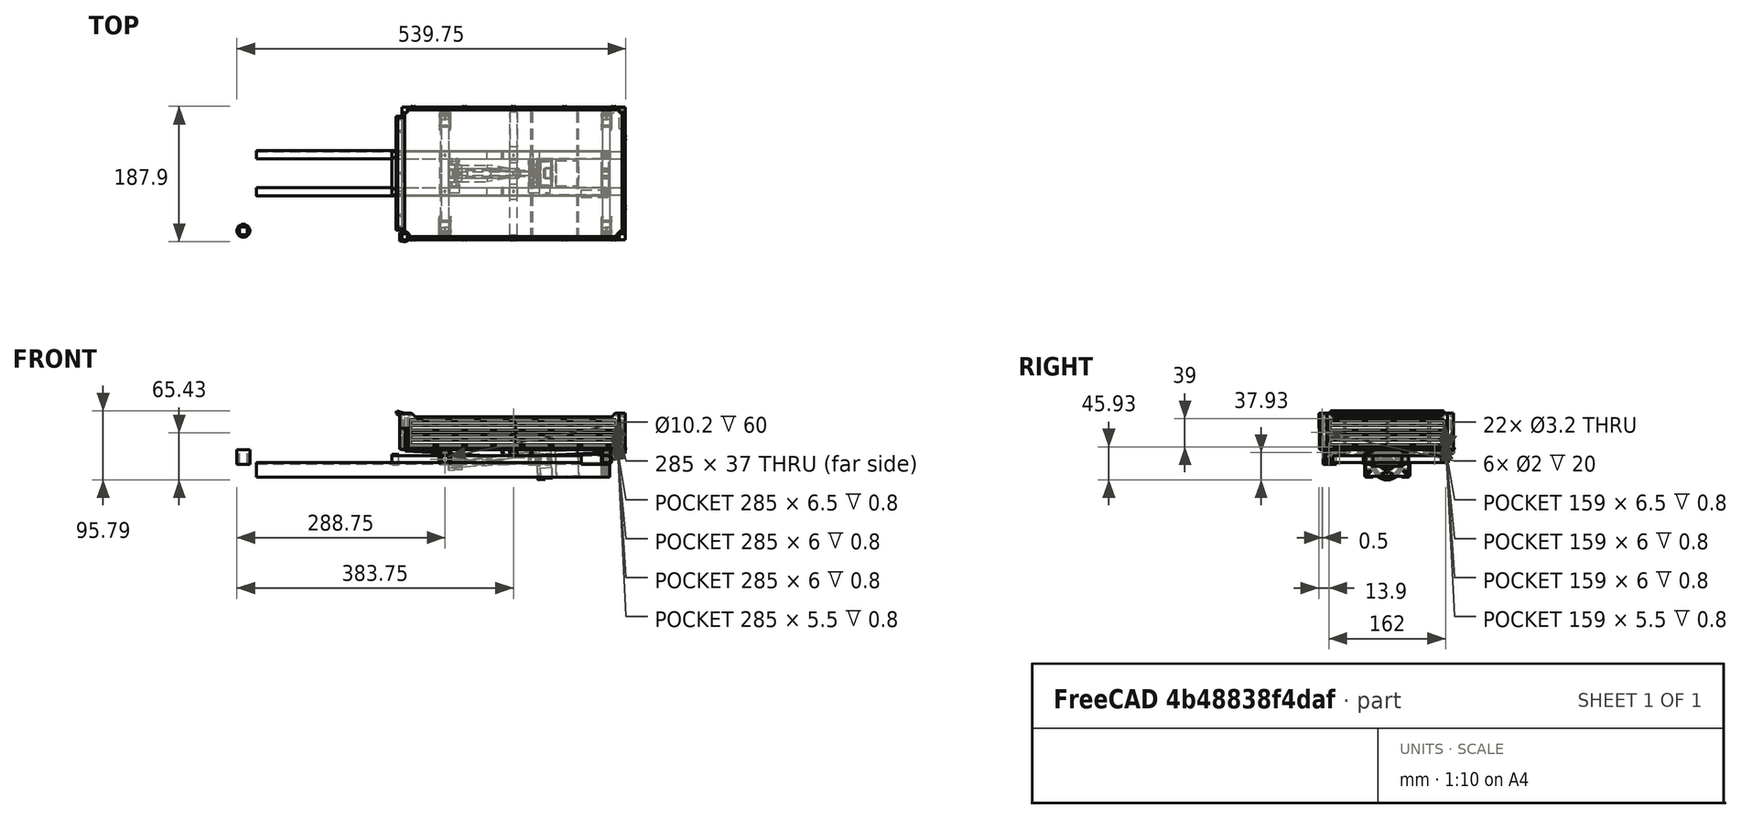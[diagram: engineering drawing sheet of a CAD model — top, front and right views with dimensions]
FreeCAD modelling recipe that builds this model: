
FCSTD DOCUMENT  (FreeCAD 0.16R6348 (Git))
Label: kipper-01
License: All rights reserved
LicenseURL: http://en.wikipedia.org/wiki/All_rights_reserved
objects: Part::Box×218, Part::Cylinder×187, Part::MultiFuse×136, Part::Cut×129, Part::Chamfer×84, Part::Fillet×63, Part::Mirroring×11, App::DocumentObjectGroup×1, Part::RegularPolygon×1, Part::Feature×1, Part::Extrusion×1
note: 831 computed .brp shape members not serialized (recipe doc carries the construction recipe); baked Part::Feature solids carry a one-line shape summary decoded from their .brp

FEATURE [Part::Box] Box416  label="Cube641"
  Height = 20
  Length = 490
  Placement = pos=(0,0,-92) rot=(0,0,1;0rad)
  Width = 11.5
FEATURE [Part::Box] Box417  label="Cube642"
  Height = 17
  Length = 490
  Placement = pos=(0,1.5,-90.5) rot=(0,0,1;0rad)
  Width = 10
FEATURE [Part::Cut] Cut429  label="Cut769"
  Base = -> Box416
  Tool = -> Box417
FEATURE [Part::Fillet] Fillet268
  Base = -> Cut429
  Edges = 2 edges r=3: [Edge11,Edge23]
  Placement = pos=(0,-1.5,0) rot=(0,0,1;0rad)
FEATURE [Part::Box] Box418  label="Cube643"
  Height = 20
  Length = 490
  Placement = pos=(0,0,-92) rot=(0,0,1;0rad)
  Width = 11.5
FEATURE [Part::Box] Box419  label="Cube644"
  Height = 17
  Length = 490
  Placement = pos=(0,1.5,-90.5) rot=(0,0,1;0rad)
  Width = 10
FEATURE [Part::Cut] Cut430  label="Cut770"
  Base = -> Box418
  Tool = -> Box419
FEATURE [Part::Fillet] Fillet269
  Base = -> Cut430
  Edges = 2 edges r=3: [Edge11,Edge23]
FEATURE [Part::Mirroring] Part__Mirroring036  label="Fillet269 (Mirror #29)"
  Base = (0,0,0)
  Normal = (0,1,0)
  Placement = pos=(0,61.5,0) rot=(0,0,1;0rad)
  Source = -> Fillet269
FEATURE [Part::MultiFuse] Fusion231  label="frame-00"
  Placement = pos=(23.5,55,74) rot=(0,0,1;0rad)
  Shapes = -> [Part__Mirroring036,Fillet268]
FEATURE [Part::Cylinder] Cylinder1019  label="Cylinder1221"
  Angle = 360
  Height = 170
  Placement = pos=(509,170,7) rot=(1,0,0;1.5708rad)
  Radius = 5
FEATURE [Part::Box] Box600  label="Cube789"
  Height = 8
  Length = 11
  Placement = pos=(279.5,0,12) rot=(0,0,1;0rad)
  Width = 170
FEATURE [Part::Box] Box601  label="Cube790"
  Height = 8
  Length = 10
  Placement = pos=(504,0,12) rot=(0,0,1;0rad)
  Width = 170
FEATURE [Part::Box] Box602  label="Cube791"
  Height = 10
  Length = 224
  Placement = pos=(290,55,2) rot=(0,0,1;0rad)
  Width = 10
FEATURE [Part::Box] Box603  label="Cube792"
  Height = 10
  Length = 224
  Placement = pos=(290,105,2) rot=(0,0,1;0rad)
  Width = 10
FEATURE [Part::Box] Box604  label="Cube793"
  Height = 8
  Length = 300
  Placement = pos=(230,55,12) rot=(0,0,1;0rad)
  Width = 10
FEATURE [Part::Box] Box605  label="Cube794"
  Height = 8
  Length = 300
  Placement = pos=(229,55,10) rot=(0,1,0;0.05236rad)
  Width = 10
FEATURE [Part::Box] Box606  label="Cube795"
  Height = 8
  Length = 300
  Placement = pos=(230,55,10) rot=(0,1,0;0.05236rad)
  Width = 10
FEATURE [Part::Mirroring] Part__Mirroring  label="Cube795 (Mirror #2)"
  Base = (0,0,0)
  Normal = (1,0,0)
  Placement = pos=(761,0,0) rot=(0,0,1;0rad)
  Source = -> Box606
FEATURE [Part::MultiFuse] Fusion
  Shapes = -> [Box605,Part__Mirroring]
FEATURE [Part::Cut] Cut
  Base = -> Box604
  Tool = -> Fusion
FEATURE [Part::Box] Box607  label="Cube796"
  Height = 8
  Length = 10
  Placement = pos=(375,0,12) rot=(0,0,1;0rad)
  Width = 170
FEATURE [Part::Box] Box608  label="Cube797"
  Height = 8
  Length = 10
  Placement = pos=(375,-1,10) rot=(-1,0,0;0.122173rad)
  Width = 170
FEATURE [Part::Box] Box609  label="Cube798"
  Height = 8
  Length = 10
  Placement = pos=(375,-1,10) rot=(-1,0,0;0.122173rad)
  Width = 170
FEATURE [Part::Mirroring] Part__Mirroring037  label="Cube798 (Mirror #3)"
  Base = (0,0,0)
  Normal = (0,1,0)
  Placement = pos=(0,170,0) rot=(0,0,1;0rad)
  Source = -> Box609
FEATURE [Part::MultiFuse] Fusion232
  Shapes = -> [Box608,Part__Mirroring037]
FEATURE [Part::Cut] Cut014188
  Base = -> Box607
  Tool = -> Fusion232
FEATURE [Part::Box] Box610  label="Cube799"
  Height = 8
  Length = 300
  Placement = pos=(230,55,12) rot=(0,0,1;0rad)
  Width = 10
FEATURE [Part::Box] Box611  label="Cube800"
  Height = 8
  Length = 300
  Placement = pos=(229,55,10) rot=(0,1,0;0.05236rad)
  Width = 10
FEATURE [Part::Box] Box612  label="Cube801"
  Height = 8
  Length = 300
  Placement = pos=(230,55,10) rot=(0,1,0;0.05236rad)
  Width = 10
FEATURE [Part::Mirroring] Part__Mirroring038  label="Cube795 (Mirror #2)001"
  Base = (0,0,0)
  Normal = (1,0,0)
  Placement = pos=(761,0,0) rot=(0,0,1;0rad)
  Source = -> Box612
FEATURE [Part::MultiFuse] Fusion233
  Shapes = -> [Box611,Part__Mirroring038]
FEATURE [Part::Cut] Cut014189
  Base = -> Box610
  Placement = pos=(0,50,0) rot=(0,0,1;0rad)
  Tool = -> Fusion233
FEATURE [Part::Box] Box112  label="Cube111"
  Height = 45
  Length = 4
  Placement = pos=(-4,-44,16) rot=(0,0,1;0rad)
  Width = 168
FEATURE [Part::Box] Box113  label="Cube112"
  Height = 33
  Length = 4
  Placement = pos=(-4,-40,22) rot=(0,0,1;0rad)
  Width = 160
FEATURE [Part::Cut] Cut166
  Base = -> Box112
  Tool = -> Box113
FEATURE [Part::Box] Box117  label="Cube116"
  Height = 7
  Length = 3
  Placement = pos=(-3,-40,35) rot=(0,0,1;0rad)
  Width = 160
FEATURE [Part::Chamfer] Chamfer048
  Base = -> Box117
  Edges = 2 edges r=1: [Edge2,Edge4]
  Placement = pos=(0,0,0.5) rot=(0,0,1;0rad)
FEATURE [Part::Cylinder] Cylinder283  label="Cylinder465"
  Angle = 360
  Height = 3.8
  Placement = pos=(-1.5,135,55) rot=(1,0,0;1.5708rad)
  Radius = 0.9
FEATURE [Part::Cylinder] Cylinder284  label="Cylinder466"
  Angle = 360
  Height = 3.8
  Placement = pos=(-1.5,135,25) rot=(1,0,0;1.5708rad)
  Radius = 0.9
FEATURE [Part::MultiFuse] Fusion161
  Placement = pos=(0,-11,0) rot=(0,0,1;0rad)
  Shapes = -> [Cylinder283,Cylinder284]
FEATURE [Part::Cylinder] Cylinder285  label="Cylinder467"
  Angle = 360
  Height = 3.8
  Placement = pos=(-1.5,135,25) rot=(1,0,0;1.5708rad)
  Radius = 0.9
FEATURE [Part::MultiFuse] Fusion162
  Placement = pos=(0,-175.2,0) rot=(0,0,1;0rad)
  Shapes = -> [Cylinder285]
FEATURE [Part::MultiFuse] Fusion163
  Placement = pos=(229,45,5) rot=(0,0,1;0rad)
  Shapes = -> [Fusion162,Fusion161]
FEATURE [Part::Box] Box121  label="kipper-front-wall-frame-ALU"
  Height = 45
  Length = 0.6
  Placement = pos=(228.4,1,21) rot=(0,0,1;0rad)
  Width = 168
FEATURE [Part::Cylinder] Cylinder290  label="Cylinder472"
  Angle = 360
  Height = 10
  Placement = pos=(227.5,111,16) rot=(0,0,1;0rad)
  Radius = 0.9
FEATURE [Part::Cylinder] Cylinder291  label="Cylinder473"
  Angle = 360
  Height = 10
  Placement = pos=(227.5,60,16) rot=(0,0,1;0rad)
  Radius = 0.9
FEATURE [Part::MultiFuse] Fusion170
  Shapes = -> [Cylinder291,Cylinder290]
FEATURE [Part::Box] Box613  label="kipper-plane002"
  Height = 1
  Length = 310
  Placement = pos=(225,-7,20) rot=(0,0,1;0rad)
  Width = 184
FEATURE [Part::Chamfer] Chamfer
  Base = -> Cut166
  Edges = 2 edges r=2: [Edge5,Edge7]
FEATURE [Part::Box] Box614  label="Cube802"
  Height = 1
  Length = 1
  Placement = pos=(-1,-40,28.5) rot=(0,0,1;0rad)
  Width = 160
FEATURE [Part::Chamfer] Chamfer064
  Base = -> Box614
  Edges = 2 edges r=0.2: [Edge2,Edge4]
  Placement = pos=(-0.6,0,0) rot=(0,0,1;0rad)
FEATURE [Part::Box] Box615  label="Cube803"
  Height = 1
  Length = 1
  Placement = pos=(-1,-40,28.5) rot=(0,0,1;0rad)
  Width = 160
FEATURE [Part::Chamfer] Chamfer065
  Base = -> Box615
  Edges = 2 edges r=0.2: [Edge2,Edge4]
  Placement = pos=(-0.6,0,20) rot=(0,0,1;0rad)
FEATURE [Part::MultiFuse] Fusion234
  Placement = pos=(229,45,5) rot=(0,0,1;0rad)
  Shapes = -> [Chamfer048,Chamfer064,Chamfer,Chamfer065]
FEATURE [Part::Box] Box111  label="Cube110"
  Height = 50
  Length = 8
  Placement = pos=(-2,124,15) rot=(0,0,1;0rad)
  Width = 8
FEATURE [Part::Box] Box122  label="Cube121"
  Height = 50
  Length = 8
  Placement = pos=(-2,-52,15) rot=(0,0,1;0rad)
  Width = 8
FEATURE [Part::MultiFuse] Fusion183
  Placement = pos=(227,45,6) rot=(0,0,1;0rad)
  Shapes = -> [Box111,Box122]
FEATURE [Part::Box] Box616  label="Cube804"
  Height = 50
  Length = 8
  Placement = pos=(-2,124,15) rot=(0,0,1;0rad)
  Width = 8
FEATURE [Part::Box] Box617  label="Cube805"
  Height = 50
  Length = 8
  Placement = pos=(-2,-52,15) rot=(0,0,1;0rad)
  Width = 8
FEATURE [Part::MultiFuse] Fusion235
  Placement = pos=(529,45,6) rot=(0,0,1;0rad)
  Shapes = -> [Box616,Box617]
FEATURE [Part::MultiFuse] Fusion236  label="kipper-walls-supports-ALU"
  Shapes = -> [Fusion235,Fusion183]
FEATURE [Part::Box] Box618  label="Cube806"
  Height = 45
  Length = 4
  Placement = pos=(-4,-44,16) rot=(0,0,1;0rad)
  Width = 293
FEATURE [Part::Box] Box619  label="Cube807"
  Height = 33
  Length = 4
  Placement = pos=(-4,-40,22) rot=(0,0,1;0rad)
  Width = 285
FEATURE [Part::Cut] Cut014193
  Base = -> Box618
  Tool = -> Box619
FEATURE [Part::Box] Box620  label="Cube808"
  Height = 7
  Length = 3
  Placement = pos=(-3,-40,35) rot=(0,0,1;0rad)
  Width = 286
FEATURE [Part::Chamfer] Chamfer066
  Base = -> Box620
  Edges = 2 edges r=1: [Edge2,Edge4]
  Placement = pos=(0,0,0.5) rot=(0,0,1;0rad)
FEATURE [Part::Chamfer] Chamfer067
  Base = -> Cut014193
  Edges = 2 edges r=2: [Edge5,Edge7]
FEATURE [Part::Box] Box621  label="Cube809"
  Height = 1
  Length = 1
  Placement = pos=(-1,-40,28.5) rot=(0,0,1;0rad)
  Width = 286
FEATURE [Part::Chamfer] Chamfer068
  Base = -> Box621
  Edges = 2 edges r=0.2: [Edge2,Edge4]
  Placement = pos=(-0.6,0,0) rot=(0,0,1;0rad)
FEATURE [Part::Box] Box622  label="Cube810"
  Height = 1
  Length = 1
  Placement = pos=(-1,-40,28.5) rot=(0,0,1;0rad)
  Width = 286
FEATURE [Part::Chamfer] Chamfer069
  Base = -> Box622
  Edges = 2 edges r=0.2: [Edge2,Edge4]
  Placement = pos=(-0.6,0,20) rot=(0,0,1;0rad)
FEATURE [Part::Box] Box623  label="kipper-side-left-wall-frame-ALU"
  Height = 42
  Length = 0.6
  Placement = pos=(526,-3.6,24) rot=(0,0,1;1.5708rad)
  Width = 292
FEATURE [Part::Box] Box158  label="Cube157"
  Height = 4
  Length = 4
  Placement = pos=(58,-53.5,14) rot=(0,0,1;0rad)
  Width = 1
FEATURE [Part::Box] Box159  label="Cube158"
  Height = 4
  Length = 6
  Placement = pos=(57,-53,14) rot=(0,0,1;0rad)
  Width = 1
FEATURE [Part::Chamfer] Chamfer059
  Base = -> Box159
  Edges = 1 edges r=0.99: [Edge10]
FEATURE [Part::Fillet] Fillet020
  Base = -> Chamfer059
  Edges = 1 edges r=0.99: [Edge8]
FEATURE [Part::Cut] Cut188
  Base = -> Fillet020
  Placement = pos=(181,45,6) rot=(0,0,1;0rad)
  Tool = -> Box158
FEATURE [Part::Box] Box160  label="Cube159"
  Height = 4
  Length = 6
  Placement = pos=(57,-53,14) rot=(0,0,1;0rad)
  Width = 1
FEATURE [Part::Chamfer] Chamfer060
  Base = -> Box160
  Edges = 1 edges r=0.99: [Edge10]
FEATURE [Part::Fillet] Fillet021
  Base = -> Chamfer060
  Edges = 1 edges r=0.99: [Edge8]
FEATURE [Part::Box] Box161  label="Cube160"
  Height = 4
  Length = 4
  Placement = pos=(58,-53.5,14) rot=(0,0,1;0rad)
  Width = 1
FEATURE [Part::Cut] Cut189
  Base = -> Fillet021
  Placement = pos=(320,45,6) rot=(0,0,1;0rad)
  Tool = -> Box161
FEATURE [Part::Box] Box162  label="Cube161"
  Height = 4
  Length = 6
  Placement = pos=(57,-53,14) rot=(0,0,1;0rad)
  Width = 1
FEATURE [Part::Chamfer] Chamfer061
  Base = -> Box162
  Edges = 1 edges r=0.99: [Edge10]
FEATURE [Part::Fillet] Fillet022
  Base = -> Chamfer061
  Edges = 1 edges r=0.99: [Edge8]
FEATURE [Part::Box] Box163  label="Cube162"
  Height = 4
  Length = 4
  Placement = pos=(58,-53.5,14) rot=(0,0,1;0rad)
  Width = 1
FEATURE [Part::Cut] Cut190
  Base = -> Fillet022
  Placement = pos=(252,45,6) rot=(0,0,1;0rad)
  Tool = -> Box163
FEATURE [Part::Box] Box164  label="Cube163"
  Height = 4
  Length = 6
  Placement = pos=(57,-53,14) rot=(0,0,1;0rad)
  Width = 1
FEATURE [Part::Chamfer] Chamfer062
  Base = -> Box164
  Edges = 1 edges r=0.99: [Edge10]
FEATURE [Part::Fillet] Fillet023
  Base = -> Chamfer062
  Edges = 1 edges r=0.99: [Edge8]
FEATURE [Part::Box] Box165  label="Cube164"
  Height = 4
  Length = 4
  Placement = pos=(58,-53.5,14) rot=(0,0,1;0rad)
  Width = 1
FEATURE [Part::Cut] Cut191
  Base = -> Fillet023
  Placement = pos=(391,45,6) rot=(0,0,1;0rad)
  Tool = -> Box165
FEATURE [Part::Box] Box166  label="Cube165"
  Height = 4
  Length = 6
  Placement = pos=(57,-53,14) rot=(0,0,1;0rad)
  Width = 1
FEATURE [Part::Chamfer] Chamfer063
  Base = -> Box166
  Edges = 1 edges r=0.99: [Edge10]
FEATURE [Part::Fillet] Fillet024
  Base = -> Chamfer063
  Edges = 1 edges r=0.99: [Edge8]
FEATURE [Part::Box] Box167  label="Cube166"
  Height = 4
  Length = 4
  Placement = pos=(58,-53.5,14) rot=(0,0,1;0rad)
  Width = 1
FEATURE [Part::Cut] Cut192
  Base = -> Fillet024
  Placement = pos=(459,45,6) rot=(0,0,1;0rad)
  Tool = -> Box167
FEATURE [Part::MultiFuse] Fusion245
  Shapes = -> [Cut188,Cut189,Cut191,Cut190,Cut192]
FEATURE [Part::Box] Box624  label="Cube811"
  Height = 45
  Length = 4
  Placement = pos=(-4,-44,16) rot=(0,0,1;0rad)
  Width = 167
FEATURE [Part::Box] Box625  label="Cube812"
  Height = 33
  Length = 4
  Placement = pos=(-4,-40,22) rot=(0,0,1;0rad)
  Width = 159
FEATURE [Part::Cut] Cut014194
  Base = -> Box624
  Tool = -> Box625
FEATURE [Part::Box] Box626  label="Cube813"
  Height = 7
  Length = 3
  Placement = pos=(-3,-40,35) rot=(0,0,1;0rad)
  Width = 160
FEATURE [Part::Chamfer] Chamfer070
  Base = -> Box626
  Edges = 2 edges r=1: [Edge2,Edge4]
  Placement = pos=(0,0,0.5) rot=(0,0,1;0rad)
FEATURE [Part::Cylinder] Cylinder1025  label="Cylinder1222"
  Angle = 360
  Height = 5
  Placement = pos=(533,6,69) rot=(1,0,0;1.5708rad)
  Radius = 0.9
FEATURE [Part::Cylinder] Cylinder1026  label="Cylinder1223"
  Angle = 360
  Height = 5
  Placement = pos=(533,168,69) rot=(1,0,0;1.5708rad)
  Radius = 0.9
FEATURE [Part::Chamfer] Chamfer071
  Base = -> Cut014194
  Edges = 2 edges r=2: [Edge5,Edge7]
FEATURE [Part::Box] Box627  label="Cube814"
  Height = 1
  Length = 1
  Placement = pos=(-1,-40,28.5) rot=(0,0,1;0rad)
  Width = 160
FEATURE [Part::Chamfer] Chamfer072
  Base = -> Box627
  Edges = 2 edges r=0.2: [Edge2,Edge4]
  Placement = pos=(-0.6,0,0) rot=(0,0,1;0rad)
FEATURE [Part::Box] Box628  label="Cube815"
  Height = 1
  Length = 1
  Placement = pos=(-1,-40,28.5) rot=(0,0,1;0rad)
  Width = 160
FEATURE [Part::Chamfer] Chamfer073
  Base = -> Box628
  Edges = 2 edges r=0.2: [Edge2,Edge4]
  Placement = pos=(-0.6,0,20) rot=(0,0,1;0rad)
FEATURE [Part::MultiFuse] Fusion251
  Placement = pos=(229,45,5) rot=(0,0,1;0rad)
  Shapes = -> [Chamfer070,Chamfer072,Chamfer071,Chamfer073]
FEATURE [Part::MultiFuse] Fusion256
  Placement = pos=(0,0,-0.5) rot=(0,0,1;0rad)
  Shapes = -> [Cylinder1025,Cylinder1026]
FEATURE [Part::Mirroring] Part__Mirroring039  label="Fusion251 (Mirror #5)"
  Base = (0,0,0)
  Normal = (1,0,0)
  Placement = pos=(760,0,0) rot=(0,0,1;0rad)
  Source = -> Fusion251
FEATURE [Part::Box] Box114  label="Cube113"
  Height = 41
  Length = 6
  Placement = pos=(223,25,21) rot=(0,0,1;0rad)
  Width = 3
FEATURE [Part::Chamfer] Chamfer076
  Base = -> Box114
  Edges = 1 edges: [Edge2 r1=8 r2=3]
FEATURE [Part::Box] Box629  label="Cube816"
  Height = 41
  Length = 6
  Placement = pos=(223,25,21) rot=(0,0,1;0rad)
  Width = 3
FEATURE [Part::Chamfer] Chamfer077
  Base = -> Box629
  Edges = 1 edges: [Edge2 r1=8 r2=3]
  Placement = pos=(0,117,0) rot=(0,0,1;0rad)
FEATURE [Part::Box] Box630  label="Cube817"
  Height = 41
  Length = 6
  Placement = pos=(223,25,21) rot=(0,0,1;0rad)
  Width = 3
FEATURE [Part::Chamfer] Chamfer078
  Base = -> Box630
  Edges = 1 edges: [Edge2 r1=8 r2=3]
  Placement = pos=(0,59,0) rot=(0,0,1;0rad)
FEATURE [Part::Cylinder] Cylinder1036  label="Cylinder1224"
  Angle = 360
  Height = 20
  Placement = pos=(10.5,10.5,0) rot=(0,0,1;0rad)
  Radius = 0.55
FEATURE [Part::Box] Box631  label="Cube818"
  Height = 20
  Length = 10.5
  Width = 10.5
FEATURE [Part::Cylinder] Cylinder1037  label="Cylinder1225"
  Angle = 360
  Height = 20
  Placement = pos=(4.1,4.1,0) rot=(0,0,1;0rad)
  Radius = 7
FEATURE [Part::Box] Box632  label="Cube819"
  Height = 20
  Length = 8.2
  Width = 8.2
FEATURE [Part::Cut] Cut014197  label="square-lathe-8mm-ADAPT"
  Base = -> Cylinder1037
  Placement = pos=(225,-7,50) rot=(0,0,1;0rad)
  Tool = -> Box632
FEATURE [Part::Box] Box633  label="Cube820"
  Height = 5
  Length = 4
  Placement = pos=(531,1,66) rot=(0,0,1;0rad)
  Width = 10
FEATURE [Part::Chamfer] Chamfer079
  Base = -> Box633
  Edges = 1 edges r=4.999: [Edge12]
FEATURE [Part::Box] Box634  label="Cube821"
  Height = 5
  Length = 4
  Placement = pos=(531,159,66) rot=(0,0,1;0rad)
  Width = 10
FEATURE [Part::Chamfer] Chamfer080
  Base = -> Box634
  Edges = 1 edges r=4.999: [Edge10]
  Placement = pos=(0,-1,0) rot=(0,0,1;0rad)
FEATURE [Part::Box] Box635  label="kipper-rear-wall-frame-ALU"
  Height = 45
  Length = 0.6
  Placement = pos=(531,1,21) rot=(0,0,1;0rad)
  Width = 167
FEATURE [Part::Box] Box636  label="Cube822"
  Height = 4
  Length = 4
  Placement = pos=(58,-53.5,14) rot=(0,0,1;0rad)
  Width = 1
FEATURE [Part::Box] Box637  label="Cube823"
  Height = 4
  Length = 6
  Placement = pos=(57,-53,14) rot=(0,0,1;0rad)
  Width = 1
FEATURE [Part::Chamfer] Chamfer081
  Base = -> Box637
  Edges = 1 edges r=0.99: [Edge10]
FEATURE [Part::Fillet] Fillet270
  Base = -> Chamfer081
  Edges = 1 edges r=0.99: [Edge8]
FEATURE [Part::Cut] Cut014199
  Base = -> Fillet270
  Placement = pos=(483,74,6) rot=(0,0,1;1.5708rad)
  Tool = -> Box636
FEATURE [Part::Box] Box638  label="Cube824"
  Height = 4
  Length = 4
  Placement = pos=(58,-53.5,14) rot=(0,0,1;0rad)
  Width = 1
FEATURE [Part::Box] Box639  label="Cube825"
  Height = 4
  Length = 6
  Placement = pos=(57,-53,14) rot=(0,0,1;0rad)
  Width = 1
FEATURE [Part::Chamfer] Chamfer082
  Base = -> Box639
  Edges = 1 edges r=0.99: [Edge10]
FEATURE [Part::Fillet] Fillet271
  Base = -> Chamfer082
  Edges = 1 edges r=0.99: [Edge8]
FEATURE [Part::Cut] Cut014200
  Base = -> Fillet271
  Placement = pos=(483,-23,6) rot=(0,0,1;1.5708rad)
  Tool = -> Box638
FEATURE [Part::Box] Box640  label="Cube826"
  Height = 5
  Length = 4
  Placement = pos=(531,1,66) rot=(0,0,1;0rad)
  Width = 10
FEATURE [Part::Chamfer] Chamfer083
  Base = -> Box640
  Edges = 1 edges r=4.999: [Edge12]
  Placement = pos=(232.5,528,0) rot=(0,0,-1;1.5708rad)
FEATURE [Part::Box] Box641  label="Cube827"
  Height = 5
  Length = 4
  Placement = pos=(531,159,66) rot=(0,0,1;0rad)
  Width = 10
FEATURE [Part::Chamfer] Chamfer084
  Base = -> Box641
  Edges = 1 edges r=4.999: [Edge10]
  Placement = pos=(357.5,528,0) rot=(0,0,-1;1.5708rad)
FEATURE [Part::Cylinder] Cylinder1048  label="Cylinder1226"
  Angle = 360
  Height = 5
  Placement = pos=(233.5,-5,68.5) rot=(0,1,0;1.5708rad)
  Radius = 0.9
FEATURE [Part::Cylinder] Cylinder1049  label="Cylinder1227"
  Angle = 360
  Height = 5
  Placement = pos=(521.5,-5,68.5) rot=(0,1,0;1.5708rad)
  Radius = 0.9
FEATURE [Part::MultiFuse] Fusion266
  Shapes = -> [Cylinder1048,Cylinder1049]
FEATURE [Part::MultiFuse] Fusion279  label="kipper-frame_"
  Shapes = -> [Cut014189,Cut014188,Cut,Box601,Box600]
FEATURE [Part::Cylinder] Cylinder1062  label="Cylinder1228"
  Angle = 360
  Height = 10
  Placement = pos=(285,8,10) rot=(0,0,1;0rad)
  Radius = 1.25
FEATURE [Part::Cylinder] Cylinder1063  label="Cylinder1229"
  Angle = 360
  Height = 10
  Placement = pos=(285,60,10) rot=(0,0,1;0rad)
  Radius = 1.25
FEATURE [Part::Cylinder] Cylinder1064  label="Cylinder1230"
  Angle = 360
  Height = 10
  Placement = pos=(285,162,10) rot=(0,0,1;0rad)
  Radius = 1.25
FEATURE [Part::Cylinder] Cylinder1065  label="Cylinder1231"
  Angle = 360
  Height = 10
  Placement = pos=(285,110,10) rot=(0,0,1;0rad)
  Radius = 1.25
FEATURE [Part::Cylinder] Cylinder1067  label="Cylinder1232"
  Angle = 360
  Height = 10
  Placement = pos=(380,60,10) rot=(0,0,1;0rad)
  Radius = 1.25
FEATURE [Part::Cylinder] Cylinder1069  label="Cylinder1233"
  Angle = 360
  Height = 10
  Placement = pos=(380,110,10) rot=(0,0,1;0rad)
  Radius = 1.25
FEATURE [Part::Cylinder] Cylinder1070  label="Cylinder1234"
  Angle = 360
  Height = 10
  Placement = pos=(509,8,10) rot=(0,0,1;0rad)
  Radius = 1.25
FEATURE [Part::Cylinder] Cylinder1071  label="Cylinder1235"
  Angle = 360
  Height = 10
  Placement = pos=(509,60,10) rot=(0,0,1;0rad)
  Radius = 1.25
FEATURE [Part::Cylinder] Cylinder1072  label="Cylinder1297"
  Angle = 360
  Height = 10
  Placement = pos=(509,162,10) rot=(0,0,1;0rad)
  Radius = 1.25
FEATURE [Part::Cylinder] Cylinder1073  label="Cylinder1298"
  Angle = 360
  Height = 10
  Placement = pos=(509,110,10) rot=(0,0,1;0rad)
  Radius = 1.25
FEATURE [Part::Cylinder] Cylinder1074  label="Cylinder1299"
  Angle = 360
  Height = 11
  Placement = pos=(279.5,4,16) rot=(0,1,0;1.5708rad)
  Radius = 1.25
FEATURE [Part::Cylinder] Cylinder1076  label="Cylinder1300"
  Angle = 360
  Height = 11
  Placement = pos=(279.5,19,16) rot=(0,1,0;1.5708rad)
  Radius = 1.25
FEATURE [Part::Cylinder] Cylinder1077  label="Cylinder1301"
  Angle = 360
  Height = 11
  Placement = pos=(503.5,19,16) rot=(0,1,0;1.5708rad)
  Radius = 1.25
FEATURE [Part::Cylinder] Cylinder1078  label="Cylinder1277"
  Angle = 360
  Height = 11
  Placement = pos=(503.5,4,16) rot=(0,1,0;1.5708rad)
  Radius = 1.25
FEATURE [Part::MultiFuse] Fusion282
  Shapes = -> [Cylinder1074,Cylinder1076,Cylinder1077,Cylinder1078]
FEATURE [Part::Cylinder] Cylinder1079  label="Cylinder1302"
  Angle = 360
  Height = 11
  Placement = pos=(279.5,4,16) rot=(0,1,0;1.5708rad)
  Radius = 1.25
FEATURE [Part::Cylinder] Cylinder1080  label="Cylinder1243"
  Angle = 360
  Height = 11
  Placement = pos=(279.5,19,16) rot=(0,1,0;1.5708rad)
  Radius = 1.25
FEATURE [Part::Cylinder] Cylinder1081  label="Cylinder1244"
  Angle = 360
  Height = 11
  Placement = pos=(503.5,19,16) rot=(0,1,0;1.5708rad)
  Radius = 1.25
FEATURE [Part::Cylinder] Cylinder1082  label="Cylinder1245"
  Angle = 360
  Height = 11
  Placement = pos=(503.5,4,16) rot=(0,1,0;1.5708rad)
  Radius = 1.25
FEATURE [Part::MultiFuse] Fusion283
  Placement = pos=(0,147,0) rot=(0,0,1;0rad)
  Shapes = -> [Cylinder1079,Cylinder1080,Cylinder1081,Cylinder1082]
FEATURE [Part::Cylinder] Cylinder1088  label="Cylinder1251"
  Angle = 360
  Height = 10
  Placement = pos=(405,105,15) rot=(-1,0,0;1.5708rad)
  Radius = 1.25
FEATURE [Part::Cylinder] Cylinder1089  label="Cylinder1252"
  Angle = 360
  Height = 10
  Placement = pos=(405,55,15) rot=(-1,0,0;1.5708rad)
  Radius = 1.25
FEATURE [Part::MultiFuse] Fusion285
  Shapes = -> [Cylinder1073,Cylinder1062,Cylinder1063,Cylinder1064,Cylinder1065,Cylinder1071,Cylinder1067,Cylinder1069,Cylinder1070,Cylinder1072]
FEATURE [Part::Box] Box  label="Cube"
  Height = 10
  Length = 145
  Placement = pos=(230,0,12) rot=(0,0,1;0rad)
  Width = 170
FEATURE [Part::Box] Box660  label="Cube845"
  Height = 10
  Length = 145
  Placement = pos=(385,0,12) rot=(0,0,1;0rad)
  Width = 170
FEATURE [Part::Box] Box661  label="Cube846"
  Height = 8
  Length = 11
  Placement = pos=(279.5,0,12) rot=(0,0,1;0rad)
  Width = 170
FEATURE [Part::Box] Box662  label="Cube847"
  Height = 8
  Length = 10
  Placement = pos=(504,0,12) rot=(0,0,1;0rad)
  Width = 170
FEATURE [Part::Box] Box663  label="Cube848"
  Height = 8
  Length = 300
  Placement = pos=(230,55,12) rot=(0,0,1;0rad)
  Width = 10
FEATURE [Part::Box] Box664  label="Cube849"
  Height = 8
  Length = 300
  Placement = pos=(229,55,10) rot=(0,1,0;0.05236rad)
  Width = 10
FEATURE [Part::Box] Box665  label="Cube850"
  Height = 8
  Length = 300
  Placement = pos=(230,55,10) rot=(0,1,0;0.05236rad)
  Width = 10
FEATURE [Part::Mirroring] Part__Mirroring041  label="Cube795 (Mirror #2)002"
  Base = (0,0,0)
  Normal = (1,0,0)
  Placement = pos=(761,0,0) rot=(0,0,1;0rad)
  Source = -> Box665
FEATURE [Part::MultiFuse] Fusion287
  Shapes = -> [Box664,Part__Mirroring041]
FEATURE [Part::Cut] Cut014212
  Base = -> Box663
  Tool = -> Fusion287
FEATURE [Part::Box] Box666  label="Cube851"
  Height = 8
  Length = 10
  Placement = pos=(375,0,12) rot=(0,0,1;0rad)
  Width = 170
FEATURE [Part::Box] Box667  label="Cube852"
  Height = 8
  Length = 10
  Placement = pos=(375,-1,10) rot=(-1,0,0;0.122173rad)
  Width = 170
FEATURE [Part::Box] Box668  label="Cube853"
  Height = 8
  Length = 10
  Placement = pos=(375,-1,10) rot=(-1,0,0;0.122173rad)
  Width = 170
FEATURE [Part::Mirroring] Part__Mirroring042  label="Cube798 (Mirror #3)001"
  Base = (0,0,0)
  Normal = (0,1,0)
  Placement = pos=(0,170,0) rot=(0,0,1;0rad)
  Source = -> Box668
FEATURE [Part::MultiFuse] Fusion288
  Shapes = -> [Box667,Part__Mirroring042]
FEATURE [Part::Cut] Cut014213
  Base = -> Box666
  Tool = -> Fusion288
FEATURE [Part::Box] Box669  label="Cube854"
  Height = 8
  Length = 300
  Placement = pos=(230,55,12) rot=(0,0,1;0rad)
  Width = 10
FEATURE [Part::Box] Box670  label="Cube855"
  Height = 8
  Length = 300
  Placement = pos=(229,55,10) rot=(0,1,0;0.05236rad)
  Width = 10
FEATURE [Part::Box] Box671  label="Cube856"
  Height = 8
  Length = 300
  Placement = pos=(230,55,10) rot=(0,1,0;0.05236rad)
  Width = 10
FEATURE [Part::Mirroring] Part__Mirroring043  label="Cube795 (Mirror #2)003"
  Base = (0,0,0)
  Normal = (1,0,0)
  Placement = pos=(761,0,0) rot=(0,0,1;0rad)
  Source = -> Box671
FEATURE [Part::MultiFuse] Fusion289
  Shapes = -> [Box670,Part__Mirroring043]
FEATURE [Part::Cut] Cut014214
  Base = -> Box669
  Placement = pos=(0,50,0) rot=(0,0,1;0rad)
  Tool = -> Fusion289
FEATURE [Part::MultiFuse] Fusion290  label="kipper-frame_001"
  Shapes = -> [Cut014214,Cut014213,Cut014212,Box662,Box661]
FEATURE [Part::Cylinder] Cylinder1090  label="Cylinder1253"
  Angle = 360
  Height = 10
  Placement = pos=(285,8,10) rot=(0,0,1;0rad)
  Radius = 1.25
FEATURE [Part::Cylinder] Cylinder1091  label="Cylinder1254"
  Angle = 360
  Height = 10
  Placement = pos=(285,60,10) rot=(0,0,1;0rad)
  Radius = 1.25
FEATURE [Part::Cylinder] Cylinder1092  label="Cylinder1255"
  Angle = 360
  Height = 10
  Placement = pos=(285,162,10) rot=(0,0,1;0rad)
  Radius = 1.25
FEATURE [Part::Cylinder] Cylinder1093  label="Cylinder1256"
  Angle = 360
  Height = 10
  Placement = pos=(285,110,10) rot=(0,0,1;0rad)
  Radius = 1.25
FEATURE [Part::Cylinder] Cylinder1094  label="Cylinder1257"
  Angle = 360
  Height = 10
  Placement = pos=(380,60,10) rot=(0,0,1;0rad)
  Radius = 1.25
FEATURE [Part::Cylinder] Cylinder1095  label="Cylinder1258"
  Angle = 360
  Height = 10
  Placement = pos=(380,110,10) rot=(0,0,1;0rad)
  Radius = 1.25
FEATURE [Part::Cylinder] Cylinder1096  label="Cylinder1259"
  Angle = 360
  Height = 10
  Placement = pos=(509,8,10) rot=(0,0,1;0rad)
  Radius = 1.25
FEATURE [Part::Cylinder] Cylinder1097  label="Cylinder1260"
  Angle = 360
  Height = 10
  Placement = pos=(509,60,10) rot=(0,0,1;0rad)
  Radius = 1.25
FEATURE [Part::Cylinder] Cylinder1098  label="Cylinder1261"
  Angle = 360
  Height = 10
  Placement = pos=(509,162,10) rot=(0,0,1;0rad)
  Radius = 1.25
FEATURE [Part::Cylinder] Cylinder1099  label="Cylinder1303"
  Angle = 360
  Height = 10
  Placement = pos=(509,110,10) rot=(0,0,1;0rad)
  Radius = 1.25
FEATURE [Part::Cylinder] Cylinder1100  label="Cylinder1304"
  Angle = 360
  Height = 11
  Placement = pos=(279.5,4,16) rot=(0,1,0;1.5708rad)
  Radius = 1.25
FEATURE [Part::Cylinder] Cylinder1101  label="Cylinder1305"
  Angle = 360
  Height = 11
  Placement = pos=(279.5,19,16) rot=(0,1,0;1.5708rad)
  Radius = 1.25
FEATURE [Part::Cylinder] Cylinder1102  label="Cylinder1306"
  Angle = 360
  Height = 11
  Placement = pos=(503.5,19,16) rot=(0,1,0;1.5708rad)
  Radius = 1.25
FEATURE [Part::Cylinder] Cylinder1103  label="Cylinder1307"
  Angle = 360
  Height = 11
  Placement = pos=(503.5,4,16) rot=(0,1,0;1.5708rad)
  Radius = 1.25
FEATURE [Part::MultiFuse] Fusion291
  Shapes = -> [Cylinder1100,Cylinder1101,Cylinder1102,Cylinder1103]
FEATURE [Part::Cylinder] Cylinder1104  label="Cylinder1308"
  Angle = 360
  Height = 11
  Placement = pos=(279.5,4,16) rot=(0,1,0;1.5708rad)
  Radius = 1.25
FEATURE [Part::Cylinder] Cylinder1105  label="Cylinder1309"
  Angle = 360
  Height = 11
  Placement = pos=(279.5,19,16) rot=(0,1,0;1.5708rad)
  Radius = 1.25
FEATURE [Part::Cylinder] Cylinder1106  label="Cylinder1310"
  Angle = 360
  Height = 11
  Placement = pos=(503.5,19,16) rot=(0,1,0;1.5708rad)
  Radius = 1.25
FEATURE [Part::Cylinder] Cylinder1107  label="Cylinder1311"
  Angle = 360
  Height = 11
  Placement = pos=(503.5,4,16) rot=(0,1,0;1.5708rad)
  Radius = 1.25
FEATURE [Part::MultiFuse] Fusion292
  Placement = pos=(0,147,0) rot=(0,0,1;0rad)
  Shapes = -> [Cylinder1104,Cylinder1105,Cylinder1106,Cylinder1107]
FEATURE [Part::Cylinder] Cylinder1111  label="Cylinder1312"
  Angle = 360
  Height = 10
  Placement = pos=(365,55,16) rot=(-1,0,0;1.5708rad)
  Radius = 1.25
FEATURE [Part::Cylinder] Cylinder1112  label="Cylinder1313"
  Angle = 360
  Height = 10
  Placement = pos=(365,105,16) rot=(-1,0,0;1.5708rad)
  Radius = 1.25
FEATURE [Part::MultiFuse] Fusion294
  Shapes = -> [Cylinder1099,Cylinder1090,Cylinder1091,Cylinder1092,Cylinder1093,Cylinder1097,Cylinder1094,Cylinder1095,Cylinder1096,Cylinder1098]
FEATURE [Part::Box] Box672  label="Cube857"
  Height = 10
  Length = 10
  Placement = pos=(375,0,12) rot=(0,0,1;0rad)
  Width = 55
FEATURE [Part::Box] Box673  label="Cube858"
  Height = 10
  Length = 10
  Placement = pos=(375,65,12) rot=(0,0,1;0rad)
  Width = 40
FEATURE [Part::Box] Box674  label="Cube859"
  Height = 10
  Length = 10
  Placement = pos=(375,115,12) rot=(0,0,1;0rad)
  Width = 55
FEATURE [Part::Box] Box675  label="Cube860"
  Height = 4.5
  Length = 10
  Placement = pos=(375,55,12) rot=(0,0,1;0rad)
  Width = 60
FEATURE [Part::MultiFuse] Fusion296
  Shapes = -> [Box672,Box674,Box675,Box673]
FEATURE [Part::Box] Box676  label="Cube861"
  Height = 4
  Length = 11
  Placement = pos=(374.5,54.5,16) rot=(0,0,1;0rad)
  Width = 11
FEATURE [Part::Box] Box677  label="Cube862"
  Height = 4
  Length = 11
  Placement = pos=(374.5,104.5,16) rot=(0,0,1;0rad)
  Width = 11
FEATURE [Part::MultiFuse] Fusion297
  Shapes = -> [Box677,Box676]
FEATURE [Part::Box] Box678  label="Cube863"
  Height = 4
  Length = 12
  Placement = pos=(217,6,70) rot=(0,1,0;0.261799rad)
  Width = 158
FEATURE [Part::Box] Box679  label="Cube864"
  Height = 4
  Length = 13
  Placement = pos=(218.588,8,70.6593) rot=(0,1,0;0.261799rad)
  Width = 154
FEATURE [Part::Box] Box680  label="Cube865"
  Height = 4
  Length = 4
  Placement = pos=(225,1,66) rot=(0,0,1;0rad)
  Width = 168
FEATURE [Part::Box] Box681  label="Cube866"
  Height = 4
  Length = 11
  Placement = pos=(218,6,66) rot=(0,0,1;0rad)
  Width = 4
FEATURE [Part::Chamfer] Chamfer097
  Base = -> Box681
  Edges = 1 edges: [Edge4 r1=3.99 r2=7]
  Placement = pos=(0,1,0) rot=(0,0,1;0rad)
FEATURE [Part::Box] Box682  label="Cube867"
  Height = 4
  Length = 11
  Placement = pos=(218,6,66) rot=(0,0,1;0rad)
  Width = 4
FEATURE [Part::Chamfer] Chamfer098
  Base = -> Box682
  Edges = 1 edges: [Edge4 r1=3.99 r2=7]
  Placement = pos=(0,153,0) rot=(0,0,1;0rad)
FEATURE [Part::Box] Box683  label="Cube868"
  Height = 4
  Length = 11
  Placement = pos=(218,6,66) rot=(0,0,1;0rad)
  Width = 4
FEATURE [Part::Chamfer] Chamfer099
  Base = -> Box683
  Edges = 1 edges: [Edge4 r1=3.99 r2=7]
  Placement = pos=(0,50,0) rot=(0,0,1;0rad)
FEATURE [Part::Box] Box684  label="Cube869"
  Height = 4
  Length = 11
  Placement = pos=(218,6,66) rot=(0,0,1;0rad)
  Width = 4
FEATURE [Part::Chamfer] Chamfer100
  Base = -> Box684
  Edges = 1 edges: [Edge4 r1=3.99 r2=7]
  Placement = pos=(0,104,0) rot=(0,0,1;0rad)
FEATURE [Part::Box] Box685  label="Cube870"
  Height = 10
  Length = 2
  Placement = pos=(229,6,63) rot=(0,0,1;0rad)
  Width = 158
FEATURE [Part::Box] Box703  label="Cube888"
  Height = 14
  Length = 40
  Placement = pos=(474,52,0) rot=(0,0,1;0rad)
  Width = 10
FEATURE [Part::Box] Box704  label="Cube889"
  Height = 10.2
  Length = 40
  Placement = pos=(474,55,1.9) rot=(0,0,1;0rad)
  Width = 10
FEATURE [Part::Cut] Cut014230
  Base = -> Box703
  Tool = -> Box704
FEATURE [Part::Cylinder] Cylinder1127  label="Cylinder1314"
  Angle = 360
  Height = 10
  Placement = pos=(509,58,7) rot=(1,0,0;1.5708rad)
  Radius = 1.5
FEATURE [Part::Cut] Cut014231  label="square-10mm-ending-HOLES"
  Base = -> Cut014230
  Tool = -> Cylinder1127
FEATURE [Part::Box] Box705  label="Cube890"
  Height = 50
  Length = 8.2
  Placement = pos=(224.9,-7,21) rot=(0,0,1;0rad)
  Width = 8
FEATURE [Part::Cylinder] Cylinder1128  label="Cylinder1315"
  Angle = 360
  Height = 10
  Placement = pos=(-1.5,135,25) rot=(1,0,0;1.5708rad)
  Radius = 1
FEATURE [Part::Cylinder] Cylinder1129  label="Cylinder1316"
  Angle = 360
  Height = 10
  Placement = pos=(-1.5,135,55) rot=(1,0,0;1.5708rad)
  Radius = 1
FEATURE [Part::MultiFuse] Fusion311
  Placement = pos=(229,-137,5) rot=(0,0,1;0rad)
  Shapes = -> [Cylinder1128,Cylinder1129]
FEATURE [Part::Cylinder] Cylinder1130  label="Cylinder1317"
  Angle = 360
  Height = 10
  Placement = pos=(220.5,-5,68.5) rot=(0,1,0;1.5708rad)
  Radius = 1
FEATURE [Part::Box] Box706  label="Cube891"
  Height = 50
  Length = 12
  Placement = pos=(223,-10,21) rot=(0,0,1;0rad)
  Width = 8
FEATURE [Part::Cut] Cut014232
  Base = -> Box706
  Tool = -> Box705
FEATURE [Part::Cylinder] Cylinder1131  label="Cylinder1318"
  Angle = 360
  Height = 10
  Placement = pos=(220.5,-1,68.5) rot=(0,1,0;1.5708rad)
  Radius = 1
FEATURE [Part::MultiFuse] Fusion312
  Shapes = -> [Cylinder1131,Cylinder1130]
FEATURE [Part::Cylinder] Cylinder1132  label="Cylinder1319"
  Angle = 360
  Height = 10
  Placement = pos=(-1.5,135,25) rot=(1,0,0;1.5708rad)
  Radius = 1
FEATURE [Part::Cylinder] Cylinder1133  label="Cylinder1320"
  Angle = 360
  Height = 10
  Placement = pos=(-1.5,135,55) rot=(1,0,0;1.5708rad)
  Radius = 1
FEATURE [Part::MultiFuse] Fusion313
  Placement = pos=(232,-137,5) rot=(0,0,1;0rad)
  Shapes = -> [Cylinder1132,Cylinder1133]
FEATURE [Part::MultiFuse] Fusion314
  Shapes = -> [Fusion311,Fusion313]
FEATURE [Part::Cut] Cut014233
  Base = -> Cut014232
  Placement = pos=(232,226,0) rot=(0,0,-1;1.5708rad)
  Tool = -> Fusion314
FEATURE [Part::Cut] Cut014234  label="square-8mm-supports-HOLES"
  Base = -> Cut014233
  Tool = -> Fusion312
FEATURE [Part::Box] Box707  label="Cube892"
  Height = 51
  Length = 149.5
  Placement = pos=(233.5,-8,20) rot=(0,0,1;0rad)
  Width = 5
FEATURE [Part::Box] Box708  label="Cube893"
  Height = 51
  Length = 143.5
  Placement = pos=(383,-8,20) rot=(0,0,1;0rad)
  Width = 5
FEATURE [Part::Box] Box728  label="Cube913"
  Height = 2
  Length = 30
  Placement = pos=(505,169,18) rot=(0,0,1;0rad)
  Width = 8
FEATURE [Part::Box] Box729  label="Cube914"
  Height = 2
  Length = 8
  Placement = pos=(527,147,18) rot=(0,0,1;0rad)
  Width = 30
FEATURE [Part::Cylinder] Cylinder1146  label="Cylinder1321"
  Angle = 360
  Height = 5
  Placement = pos=(531,173,15) rot=(0,0,1;0rad)
  Radius = 4
FEATURE [Part::Cylinder] Cylinder1147  label="Cylinder1322"
  Angle = 360
  Height = 10
  Placement = pos=(531,173,15) rot=(0,0,1;0rad)
  Radius = 1.5
FEATURE [Part::MultiFuse] Fusion330
  Shapes = -> [Box728,Cylinder1146,Box729]
FEATURE [Part::Cut] Cut014247  label="kipper-corners-HOLES"
  Base = -> Fusion330
  Tool = -> Cylinder1147
FEATURE [Part::Cylinder] Cylinder1148  label="Cylinder1323"
  Angle = 360
  Height = 20
  Placement = pos=(5.25,5.25,0) rot=(0,0,1;0rad)
  Radius = 9
FEATURE [Part::Cylinder] Cylinder1149  label="Cylinder1324"
  Angle = 360
  Height = 20
  Placement = pos=(0,10.5,0) rot=(0,0,1;0rad)
  Radius = 0.55
FEATURE [Part::Cylinder] Cylinder1150  label="Cylinder1325"
  Angle = 360
  Height = 20
  Radius = 0.55
FEATURE [Part::Cylinder] Cylinder1151  label="Cylinder1326"
  Angle = 360
  Height = 20
  Placement = pos=(10.5,0,0) rot=(0,0,1;0rad)
  Radius = 0.55
FEATURE [Part::MultiFuse] Fusion331
  Shapes = -> [Cylinder1036,Box631,Cylinder1151,Cylinder1149,Cylinder1150]
FEATURE [Part::Cut] Cut014248
  Base = -> Cylinder1148
  Tool = -> Fusion331
FEATURE [Part::Fillet] Fillet287  label="square-lathe-10mm-ADAPT"
  Base = -> Cut014248
  Edges = 8 edges r=1: [Edge24,Edge25,Edge26,Edge27,Edge28,Edge29,Edge30,Edge31]
FEATURE [App::DocumentObjectGroup] Group  label="Tools"
  Group = -> [Cut014197,Cut014231,Cut014234,Cut014247,Fillet287]
FEATURE [Part::Box] Box730  label="Cube915"
  Height = 18
  Length = 2
  Placement = pos=(502,0,2) rot=(0,0,1;0rad)
  Width = 10
FEATURE [Part::Box] Box731  label="Cube916"
  Height = 8
  Length = 2
  Placement = pos=(502,10,12) rot=(0,0,1;0rad)
  Width = 15
FEATURE [Part::MultiFuse] Fusion332
  Shapes = -> [Box730,Box731]
FEATURE [Part::Cylinder] Cylinder1152  label="Cylinder1327"
  Angle = 360
  Height = 10
  Placement = pos=(500,5,7) rot=(0,1,0;1.5708rad)
  Radius = 1.75
FEATURE [Part::Cut] Cut014251
  Base = -> Fusion332
  Tool = -> Cylinder1152
FEATURE [Part::Cylinder] Cylinder1153  label="Cylinder1328"
  Angle = 360
  Height = 10
  Placement = pos=(504,4,16) rot=(0,1,0;1.5708rad)
  Radius = 1.6
FEATURE [Part::Cylinder] Cylinder1154  label="Cylinder1329"
  Angle = 360
  Height = 10
  Placement = pos=(504,19,16) rot=(0,1,0;1.5708rad)
  Radius = 1.6
FEATURE [Part::MultiFuse] Fusion333
  Placement = pos=(-4,0,0) rot=(0,0,1;0rad)
  Shapes = -> [Cylinder1154,Cylinder1153]
FEATURE [Part::Cut] Cut014252
  Base = -> Cut014251
  Tool = -> Fusion333
FEATURE [Part::Fillet] Fillet290
  Base = -> Cut014252
  Edges = 2 edges r=4: [Edge1,Edge6]
FEATURE [Part::Fillet] Fillet291  label="kipper-lock-front-00"
  Base = -> Fillet290
  Edges = 3 edges r=2: [Edge3,Edge17,Edge28]
FEATURE [Part::MultiFuse] Fusion335
  Shapes = -> [Box685,Box679]
FEATURE [Part::MultiFuse] Fusion337
  Shapes = -> [Box635,Chamfer080,Chamfer079,Part__Mirroring039]
FEATURE [Part::Cut] Cut014254
  Base = -> Fusion337
  Tool = -> Fusion256
FEATURE [Part::MultiFuse] Fusion339
  Shapes = -> [Fusion163,Fusion170]
FEATURE [Part::MultiFuse] Fusion340
  Shapes = -> [Box121,Fusion234]
FEATURE [Part::Cut] Cut014255
  Base = -> Fusion340
  Tool = -> Fusion339
FEATURE [Part::MultiFuse] Fusion341
  Shapes = -> [Cut014255,Chamfer078,Chamfer077,Chamfer076]
FEATURE [Part::MultiFuse] Fusion342
  Shapes = -> [Box680,Box678,Chamfer097,Chamfer098,Chamfer100,Chamfer099]
FEATURE [Part::Cut] Cut014256
  Base = -> Fusion342
  Tool = -> Fusion335
FEATURE [Part::MultiFuse] Fusion343  label="kipper-front-wall"
  Shapes = -> [Cut014256,Fusion341]
FEATURE [Part::MultiFuse] Fusion344
  Shapes = -> [Cut014254,Cut014199,Cut014200]
FEATURE [Part::Chamfer] Chamfer125
  Base = -> Fusion344
  Edges = 1 edges: [Edge8 r1=1.5 r2=3]
  Placement = pos=(0,0.5,0) rot=(0,0,1;0rad)
FEATURE [Part::MultiFuse] Fusion244
  Placement = pos=(482.5,-3,5) rot=(0,0,1;1.5708rad)
  Shapes = -> [Chamfer066,Chamfer068,Chamfer067,Chamfer069]
FEATURE [Part::MultiFuse] Fusion345
  Shapes = -> [Box623,Chamfer084,Chamfer083,Fusion245,Fusion244]
FEATURE [Part::Cut] Cut014257
  Base = -> Fusion345
  Tool = -> Fusion266
FEATURE [Part::Chamfer] Chamfer126
  Base = -> Cut014257
  Edges = 1 edges: [Edge41 r1=1.5 r2=3]
FEATURE [Part::Box] Box750  label="Cube934"
  Height = 45
  Length = 4
  Placement = pos=(-4,-44,16) rot=(0,0,1;0rad)
  Width = 293
FEATURE [Part::Box] Box751  label="Cube935"
  Height = 33
  Length = 4
  Placement = pos=(-4,-40,22) rot=(0,0,1;0rad)
  Width = 285
FEATURE [Part::Cut] Cut014265
  Base = -> Box750
  Tool = -> Box751
FEATURE [Part::Box] Box752  label="Cube936"
  Height = 7
  Length = 3
  Placement = pos=(-3,-40,35) rot=(0,0,1;0rad)
  Width = 286
FEATURE [Part::Chamfer] Chamfer139
  Base = -> Box752
  Edges = 2 edges r=1: [Edge2,Edge4]
  Placement = pos=(0,0,0.5) rot=(0,0,1;0rad)
FEATURE [Part::Chamfer] Chamfer140
  Base = -> Cut014265
  Edges = 2 edges r=2: [Edge5,Edge7]
FEATURE [Part::Box] Box753  label="Cube937"
  Height = 1
  Length = 1
  Placement = pos=(-1,-40,28.5) rot=(0,0,1;0rad)
  Width = 286
FEATURE [Part::Chamfer] Chamfer141
  Base = -> Box753
  Edges = 2 edges r=0.2: [Edge2,Edge4]
  Placement = pos=(-0.6,0,0) rot=(0,0,1;0rad)
FEATURE [Part::Box] Box754  label="Cube938"
  Height = 1
  Length = 1
  Placement = pos=(-1,-40,28.5) rot=(0,0,1;0rad)
  Width = 286
FEATURE [Part::Chamfer] Chamfer142
  Base = -> Box754
  Edges = 2 edges r=0.2: [Edge2,Edge4]
  Placement = pos=(-0.6,0,20) rot=(0,0,1;0rad)
FEATURE [Part::Box] Box755  label="kipper-side-left-wall-frame-ALU002"
  Height = 42
  Length = 0.6
  Placement = pos=(526,-3.6,24) rot=(0,0,1;1.5708rad)
  Width = 292
FEATURE [Part::Box] Box756  label="Cube939"
  Height = 4
  Length = 4
  Placement = pos=(58,-53.5,14) rot=(0,0,1;0rad)
  Width = 1
FEATURE [Part::Box] Box757  label="Cube940"
  Height = 4
  Length = 6
  Placement = pos=(57,-53,14) rot=(0,0,1;0rad)
  Width = 1
FEATURE [Part::Chamfer] Chamfer143
  Base = -> Box757
  Edges = 1 edges r=0.99: [Edge10]
FEATURE [Part::Fillet] Fillet300
  Base = -> Chamfer143
  Edges = 1 edges r=0.99: [Edge8]
FEATURE [Part::Cut] Cut014266
  Base = -> Fillet300
  Placement = pos=(181,45,6) rot=(0,0,1;0rad)
  Tool = -> Box756
FEATURE [Part::Box] Box758  label="Cube941"
  Height = 4
  Length = 6
  Placement = pos=(57,-53,14) rot=(0,0,1;0rad)
  Width = 1
FEATURE [Part::Chamfer] Chamfer144
  Base = -> Box758
  Edges = 1 edges r=0.99: [Edge10]
FEATURE [Part::Fillet] Fillet301
  Base = -> Chamfer144
  Edges = 1 edges r=0.99: [Edge8]
FEATURE [Part::Box] Box759  label="Cube942"
  Height = 4
  Length = 4
  Placement = pos=(58,-53.5,14) rot=(0,0,1;0rad)
  Width = 1
FEATURE [Part::Cut] Cut014267
  Base = -> Fillet301
  Placement = pos=(320,45,6) rot=(0,0,1;0rad)
  Tool = -> Box759
FEATURE [Part::Box] Box760  label="Cube943"
  Height = 4
  Length = 6
  Placement = pos=(57,-53,14) rot=(0,0,1;0rad)
  Width = 1
FEATURE [Part::Chamfer] Chamfer145
  Base = -> Box760
  Edges = 1 edges r=0.99: [Edge10]
FEATURE [Part::Fillet] Fillet302
  Base = -> Chamfer145
  Edges = 1 edges r=0.99: [Edge8]
FEATURE [Part::Box] Box761  label="Cube944"
  Height = 4
  Length = 4
  Placement = pos=(58,-53.5,14) rot=(0,0,1;0rad)
  Width = 1
FEATURE [Part::Cut] Cut014268
  Base = -> Fillet302
  Placement = pos=(252,45,6) rot=(0,0,1;0rad)
  Tool = -> Box761
FEATURE [Part::Box] Box762  label="Cube945"
  Height = 4
  Length = 6
  Placement = pos=(57,-53,14) rot=(0,0,1;0rad)
  Width = 1
FEATURE [Part::Chamfer] Chamfer146
  Base = -> Box762
  Edges = 1 edges r=0.99: [Edge10]
FEATURE [Part::Fillet] Fillet303
  Base = -> Chamfer146
  Edges = 1 edges r=0.99: [Edge8]
FEATURE [Part::Box] Box763  label="Cube946"
  Height = 4
  Length = 4
  Placement = pos=(58,-53.5,14) rot=(0,0,1;0rad)
  Width = 1
FEATURE [Part::Cut] Cut014269
  Base = -> Fillet303
  Placement = pos=(391,45,6) rot=(0,0,1;0rad)
  Tool = -> Box763
FEATURE [Part::Box] Box764  label="Cube947"
  Height = 4
  Length = 6
  Placement = pos=(57,-53,14) rot=(0,0,1;0rad)
  Width = 1
FEATURE [Part::Chamfer] Chamfer147
  Base = -> Box764
  Edges = 1 edges r=0.99: [Edge10]
FEATURE [Part::Fillet] Fillet304
  Base = -> Chamfer147
  Edges = 1 edges r=0.99: [Edge8]
FEATURE [Part::Box] Box765  label="Cube948"
  Height = 4
  Length = 4
  Placement = pos=(58,-53.5,14) rot=(0,0,1;0rad)
  Width = 1
FEATURE [Part::Cut] Cut014270
  Base = -> Fillet304
  Placement = pos=(459,45,6) rot=(0,0,1;0rad)
  Tool = -> Box765
FEATURE [Part::MultiFuse] Fusion350
  Shapes = -> [Cut014266,Cut014267,Cut014269,Cut014268,Cut014270]
FEATURE [Part::Box] Box766  label="Cube949"
  Height = 5
  Length = 4
  Placement = pos=(531,1,66) rot=(0,0,1;0rad)
  Width = 10
FEATURE [Part::Chamfer] Chamfer148
  Base = -> Box766
  Edges = 1 edges r=4.999: [Edge12]
  Placement = pos=(232.5,528,0) rot=(0,0,-1;1.5708rad)
FEATURE [Part::Box] Box767  label="Cube950"
  Height = 5
  Length = 4
  Placement = pos=(531,159,66) rot=(0,0,1;0rad)
  Width = 10
FEATURE [Part::Chamfer] Chamfer149
  Base = -> Box767
  Edges = 1 edges r=4.999: [Edge10]
  Placement = pos=(357.5,528,0) rot=(0,0,-1;1.5708rad)
FEATURE [Part::Cylinder] Cylinder1157  label="Cylinder1330"
  Angle = 360
  Height = 5
  Placement = pos=(233.5,-5,68.5) rot=(0,1,0;1.5708rad)
  Radius = 0.9
FEATURE [Part::Cylinder] Cylinder1158  label="Cylinder1331"
  Angle = 360
  Height = 5
  Placement = pos=(521.5,-5,68.5) rot=(0,1,0;1.5708rad)
  Radius = 0.9
FEATURE [Part::MultiFuse] Fusion351
  Shapes = -> [Cylinder1157,Cylinder1158]
FEATURE [Part::MultiFuse] Fusion352
  Placement = pos=(482.5,-3,5) rot=(0,0,1;1.5708rad)
  Shapes = -> [Chamfer139,Chamfer141,Chamfer140,Chamfer142]
FEATURE [Part::MultiFuse] Fusion353
  Shapes = -> [Box755,Chamfer149,Chamfer148,Fusion350,Fusion352]
FEATURE [Part::Cut] Cut014271
  Base = -> Fusion353
  Tool = -> Fusion351
FEATURE [Part::Chamfer] Chamfer150
  Base = -> Cut014271
  Edges = 1 edges: [Edge41 r1=1.5 r2=3]
FEATURE [Part::Fillet] Fillet305  label="kipper-side-wall-00"
  Base = -> Chamfer150
  Edges = 1 edges r=2: [Edge16]
FEATURE [Part::Box] Box768  label="Cube951"
  Height = 45
  Length = 4
  Placement = pos=(-4,-44,16) rot=(0,0,1;0rad)
  Width = 293
FEATURE [Part::Box] Box769  label="Cube952"
  Height = 33
  Length = 4
  Placement = pos=(-4,-40,22) rot=(0,0,1;0rad)
  Width = 285
FEATURE [Part::Cut] Cut014272
  Base = -> Box768
  Tool = -> Box769
FEATURE [Part::Box] Box770  label="Cube953"
  Height = 7
  Length = 3
  Placement = pos=(-3,-40,35) rot=(0,0,1;0rad)
  Width = 286
FEATURE [Part::Chamfer] Chamfer151
  Base = -> Box770
  Edges = 2 edges r=1: [Edge2,Edge4]
  Placement = pos=(0,0,0.5) rot=(0,0,1;0rad)
FEATURE [Part::Chamfer] Chamfer152
  Base = -> Cut014272
  Edges = 2 edges r=2: [Edge5,Edge7]
FEATURE [Part::Box] Box771  label="Cube954"
  Height = 1
  Length = 1
  Placement = pos=(-1,-40,28.5) rot=(0,0,1;0rad)
  Width = 286
FEATURE [Part::Chamfer] Chamfer153
  Base = -> Box771
  Edges = 2 edges r=0.2: [Edge2,Edge4]
  Placement = pos=(-0.6,0,0) rot=(0,0,1;0rad)
FEATURE [Part::Box] Box772  label="Cube955"
  Height = 1
  Length = 1
  Placement = pos=(-1,-40,28.5) rot=(0,0,1;0rad)
  Width = 286
FEATURE [Part::Chamfer] Chamfer154
  Base = -> Box772
  Edges = 2 edges r=0.2: [Edge2,Edge4]
  Placement = pos=(-0.6,0,20) rot=(0,0,1;0rad)
FEATURE [Part::Box] Box773  label="kipper-side-left-wall-frame-ALU003"
  Height = 42
  Length = 0.6
  Placement = pos=(526,-3.6,24) rot=(0,0,1;1.5708rad)
  Width = 292
FEATURE [Part::Box] Box774  label="Cube956"
  Height = 4
  Length = 4
  Placement = pos=(58,-53.5,14) rot=(0,0,1;0rad)
  Width = 1
FEATURE [Part::Box] Box775  label="Cube957"
  Height = 4
  Length = 6
  Placement = pos=(57,-53,14) rot=(0,0,1;0rad)
  Width = 1
FEATURE [Part::Chamfer] Chamfer155
  Base = -> Box775
  Edges = 1 edges r=0.99: [Edge10]
FEATURE [Part::Fillet] Fillet306
  Base = -> Chamfer155
  Edges = 1 edges r=0.99: [Edge8]
FEATURE [Part::Cut] Cut014273
  Base = -> Fillet306
  Placement = pos=(181,45,6) rot=(0,0,1;0rad)
  Tool = -> Box774
FEATURE [Part::Box] Box776  label="Cube958"
  Height = 4
  Length = 6
  Placement = pos=(57,-53,14) rot=(0,0,1;0rad)
  Width = 1
FEATURE [Part::Chamfer] Chamfer156
  Base = -> Box776
  Edges = 1 edges r=0.99: [Edge10]
FEATURE [Part::Fillet] Fillet307
  Base = -> Chamfer156
  Edges = 1 edges r=0.99: [Edge8]
FEATURE [Part::Box] Box777  label="Cube959"
  Height = 4
  Length = 4
  Placement = pos=(58,-53.5,14) rot=(0,0,1;0rad)
  Width = 1
FEATURE [Part::Cut] Cut014274
  Base = -> Fillet307
  Placement = pos=(320,45,6) rot=(0,0,1;0rad)
  Tool = -> Box777
FEATURE [Part::Box] Box778  label="Cube960"
  Height = 4
  Length = 6
  Placement = pos=(57,-53,14) rot=(0,0,1;0rad)
  Width = 1
FEATURE [Part::Chamfer] Chamfer157
  Base = -> Box778
  Edges = 1 edges r=0.99: [Edge10]
FEATURE [Part::Fillet] Fillet308
  Base = -> Chamfer157
  Edges = 1 edges r=0.99: [Edge8]
FEATURE [Part::Box] Box779  label="Cube961"
  Height = 4
  Length = 4
  Placement = pos=(58,-53.5,14) rot=(0,0,1;0rad)
  Width = 1
FEATURE [Part::Cut] Cut014275
  Base = -> Fillet308
  Placement = pos=(252,45,6) rot=(0,0,1;0rad)
  Tool = -> Box779
FEATURE [Part::Box] Box780  label="Cube962"
  Height = 4
  Length = 6
  Placement = pos=(57,-53,14) rot=(0,0,1;0rad)
  Width = 1
FEATURE [Part::Chamfer] Chamfer158
  Base = -> Box780
  Edges = 1 edges r=0.99: [Edge10]
FEATURE [Part::Fillet] Fillet309
  Base = -> Chamfer158
  Edges = 1 edges r=0.99: [Edge8]
FEATURE [Part::Box] Box781  label="Cube963"
  Height = 4
  Length = 4
  Placement = pos=(58,-53.5,14) rot=(0,0,1;0rad)
  Width = 1
FEATURE [Part::Cut] Cut014276
  Base = -> Fillet309
  Placement = pos=(391,45,6) rot=(0,0,1;0rad)
  Tool = -> Box781
FEATURE [Part::Box] Box782  label="Cube964"
  Height = 4
  Length = 6
  Placement = pos=(57,-53,14) rot=(0,0,1;0rad)
  Width = 1
FEATURE [Part::Chamfer] Chamfer159
  Base = -> Box782
  Edges = 1 edges r=0.99: [Edge10]
FEATURE [Part::Fillet] Fillet310
  Base = -> Chamfer159
  Edges = 1 edges r=0.99: [Edge8]
FEATURE [Part::Box] Box783  label="Cube965"
  Height = 4
  Length = 4
  Placement = pos=(58,-53.5,14) rot=(0,0,1;0rad)
  Width = 1
FEATURE [Part::Cut] Cut014277
  Base = -> Fillet310
  Placement = pos=(459,45,6) rot=(0,0,1;0rad)
  Tool = -> Box783
FEATURE [Part::MultiFuse] Fusion354
  Shapes = -> [Cut014273,Cut014274,Cut014276,Cut014275,Cut014277]
FEATURE [Part::Box] Box784  label="Cube966"
  Height = 5
  Length = 4
  Placement = pos=(531,1,66) rot=(0,0,1;0rad)
  Width = 10
FEATURE [Part::Chamfer] Chamfer160
  Base = -> Box784
  Edges = 1 edges r=4.999: [Edge12]
  Placement = pos=(232.5,528,0) rot=(0,0,-1;1.5708rad)
FEATURE [Part::Box] Box785  label="Cube967"
  Height = 5
  Length = 4
  Placement = pos=(531,159,66) rot=(0,0,1;0rad)
  Width = 10
FEATURE [Part::Chamfer] Chamfer161
  Base = -> Box785
  Edges = 1 edges r=4.999: [Edge10]
  Placement = pos=(357.5,528,0) rot=(0,0,-1;1.5708rad)
FEATURE [Part::Cylinder] Cylinder1159  label="Cylinder1332"
  Angle = 360
  Height = 5
  Placement = pos=(233.5,-5,68.5) rot=(0,1,0;1.5708rad)
  Radius = 0.9
FEATURE [Part::Cylinder] Cylinder1160  label="Cylinder1333"
  Angle = 360
  Height = 5
  Placement = pos=(521.5,-5,68.5) rot=(0,1,0;1.5708rad)
  Radius = 0.9
FEATURE [Part::MultiFuse] Fusion355
  Shapes = -> [Cylinder1159,Cylinder1160]
FEATURE [Part::MultiFuse] Fusion356
  Placement = pos=(482.5,-3,5) rot=(0,0,1;1.5708rad)
  Shapes = -> [Chamfer151,Chamfer153,Chamfer152,Chamfer154]
FEATURE [Part::MultiFuse] Fusion357
  Shapes = -> [Box773,Chamfer161,Chamfer160,Fusion354,Fusion356]
FEATURE [Part::Cut] Cut014278
  Base = -> Fusion357
  Tool = -> Fusion355
FEATURE [Part::Chamfer] Chamfer162
  Base = -> Cut014278
  Edges = 1 edges: [Edge41 r1=1.5 r2=3]
FEATURE [Part::Fillet] Fillet311  label="kipper-side-wall-01"
  Base = -> Chamfer162
  Edges = 1 edges r=2: [Edge16]
FEATURE [Part::Cut] Cut014279
  Base = -> Fillet305
  Tool = -> Box708
FEATURE [Part::Cut] Cut014280
  Base = -> Fillet311
  Tool = -> Box707
FEATURE [Part::Cylinder] Cylinder
  Angle = 360
  Height = 40
  Placement = pos=(363,-5,24) rot=(0,1,0;1.5708rad)
  Radius = 1
FEATURE [Part::Cylinder] Cylinder1161
  Angle = 360
  Height = 40
  Placement = pos=(363,-5,63) rot=(0,1,0;1.5708rad)
  Radius = 1
FEATURE [Part::Cylinder] Cylinder1162
  Angle = 360
  Height = 40
  Placement = pos=(363,-4.5,44) rot=(0,1,0;1.5708rad)
  Radius = 1
FEATURE [Part::MultiFuse] Fusion358
  Shapes = -> [Cylinder,Cylinder1162,Cylinder1161]
FEATURE [Part::Cylinder] Cylinder1163
  Angle = 360
  Height = 40
  Placement = pos=(363,-5,24) rot=(0,1,0;1.5708rad)
  Radius = 1
FEATURE [Part::Cylinder] Cylinder1164
  Angle = 360
  Height = 40
  Placement = pos=(363,-5,63) rot=(0,1,0;1.5708rad)
  Radius = 1
FEATURE [Part::Cylinder] Cylinder1165
  Angle = 360
  Height = 40
  Placement = pos=(363,-4.5,44) rot=(0,1,0;1.5708rad)
  Radius = 1
FEATURE [Part::MultiFuse] Fusion359
  Shapes = -> [Cylinder1163,Cylinder1165,Cylinder1164]
FEATURE [Part::Box] Box786  label="Cube968"
  Height = 10
  Length = 8
  Placement = pos=(527,-7,21) rot=(0,0,1;0rad)
  Width = 8
FEATURE [Part::Box] Box787  label="Cube969"
  Height = 5
  Length = 8
  Placement = pos=(523,-3,21) rot=(0,0,1;0rad)
  Width = 8
FEATURE [Part::Chamfer] Chamfer164
  Base = -> Box787
  Edges = 1 edges r=5: [Edge3]
FEATURE [Part::Cylinder] Cylinder1166  label="Cylinder1334"
  Angle = 360
  Height = 2
  Placement = pos=(525,-3,24) rot=(-1,0,0;1.5708rad)
  Radius = 1.6
FEATURE [Part::Cylinder] Cylinder1167  label="Cylinder1335"
  Angle = 360
  Height = 2
  Placement = pos=(529,3,24) rot=(0,1,0;1.5708rad)
  Radius = 1.6
FEATURE [Part::MultiFuse] Fusion360
  Shapes = -> [Cylinder1167,Cylinder1166]
FEATURE [Part::Fillet] Fillet312
  Base = -> Chamfer164
  Edges = 5 edges r=2: [Edge1,Edge2,Edge5,Edge7,Edge10]
FEATURE [Part::Cut] Cut014283
  Base = -> Fillet312
  Tool = -> Fusion360
FEATURE [Part::Cut] Cut014284  label="kipper-magnets-holder"
  Base = -> Cut014283
  Tool = -> Box786
FEATURE [Part::Cylinder] Cylinder1168  label="Cylinder1336"
  Angle = 360
  Height = 2
  Placement = pos=(531,3,24) rot=(0,1,0;1.5708rad)
  Radius = 1.6
FEATURE [Part::Cylinder] Cylinder1169  label="Cylinder1337"
  Angle = 360
  Height = 2
  Placement = pos=(525,-5,24) rot=(-1,0,0;1.5708rad)
  Radius = 1.6
FEATURE [Part::Cylinder] Cylinder1170  label="Cylinder1338"
  Angle = 360
  Height = 2
  Placement = pos=(235,-5,24) rot=(-1,0,0;1.5708rad)
  Radius = 1.6
FEATURE [Part::MultiFuse] Fusion361
  Shapes = -> [Cylinder1169,Cylinder1170]
FEATURE [Part::Cut] Cut014285
  Base = -> Chamfer126
  Tool = -> Fusion361
FEATURE [Part::Fillet] Fillet313  label="kipper-left-side-wall"
  Base = -> Cut014285
  Edges = 1 edges r=2: [Edge5]
FEATURE [Part::Box] Box788  label="Cube970"
  Height = 45
  Length = 4
  Placement = pos=(-4,-44,16) rot=(0,0,1;0rad)
  Width = 293
FEATURE [Part::Box] Box789  label="Cube971"
  Height = 33
  Length = 4
  Placement = pos=(-4,-40,22) rot=(0,0,1;0rad)
  Width = 285
FEATURE [Part::Cut] Cut014286
  Base = -> Box788
  Tool = -> Box789
FEATURE [Part::Box] Box790  label="Cube972"
  Height = 7
  Length = 3
  Placement = pos=(-3,-40,35) rot=(0,0,1;0rad)
  Width = 286
FEATURE [Part::Chamfer] Chamfer165
  Base = -> Box790
  Edges = 2 edges r=1: [Edge2,Edge4]
  Placement = pos=(0,0,0.5) rot=(0,0,1;0rad)
FEATURE [Part::Chamfer] Chamfer166
  Base = -> Cut014286
  Edges = 2 edges r=2: [Edge5,Edge7]
FEATURE [Part::Box] Box791  label="Cube973"
  Height = 1
  Length = 1
  Placement = pos=(-1,-40,28.5) rot=(0,0,1;0rad)
  Width = 286
FEATURE [Part::Chamfer] Chamfer167
  Base = -> Box791
  Edges = 2 edges r=0.2: [Edge2,Edge4]
  Placement = pos=(-0.6,0,0) rot=(0,0,1;0rad)
FEATURE [Part::Box] Box792  label="Cube974"
  Height = 1
  Length = 1
  Placement = pos=(-1,-40,28.5) rot=(0,0,1;0rad)
  Width = 286
FEATURE [Part::Chamfer] Chamfer168
  Base = -> Box792
  Edges = 2 edges r=0.2: [Edge2,Edge4]
  Placement = pos=(-0.6,0,20) rot=(0,0,1;0rad)
FEATURE [Part::Box] Box793  label="kipper-side-left-wall-frame-ALU004"
  Height = 42
  Length = 0.6
  Placement = pos=(526,-3.6,24) rot=(0,0,1;1.5708rad)
  Width = 292
FEATURE [Part::Box] Box794  label="Cube975"
  Height = 4
  Length = 4
  Placement = pos=(58,-53.5,14) rot=(0,0,1;0rad)
  Width = 1
FEATURE [Part::Box] Box795  label="Cube976"
  Height = 4
  Length = 6
  Placement = pos=(57,-53,14) rot=(0,0,1;0rad)
  Width = 1
FEATURE [Part::Chamfer] Chamfer169
  Base = -> Box795
  Edges = 1 edges r=0.99: [Edge10]
FEATURE [Part::Fillet] Fillet314
  Base = -> Chamfer169
  Edges = 1 edges r=0.99: [Edge8]
FEATURE [Part::Cut] Cut014287
  Base = -> Fillet314
  Placement = pos=(181,45,6) rot=(0,0,1;0rad)
  Tool = -> Box794
FEATURE [Part::Box] Box796  label="Cube977"
  Height = 4
  Length = 6
  Placement = pos=(57,-53,14) rot=(0,0,1;0rad)
  Width = 1
FEATURE [Part::Chamfer] Chamfer170
  Base = -> Box796
  Edges = 1 edges r=0.99: [Edge10]
FEATURE [Part::Fillet] Fillet315
  Base = -> Chamfer170
  Edges = 1 edges r=0.99: [Edge8]
FEATURE [Part::Box] Box797  label="Cube978"
  Height = 4
  Length = 4
  Placement = pos=(58,-53.5,14) rot=(0,0,1;0rad)
  Width = 1
FEATURE [Part::Cut] Cut014288
  Base = -> Fillet315
  Placement = pos=(320,45,6) rot=(0,0,1;0rad)
  Tool = -> Box797
FEATURE [Part::Box] Box798  label="Cube979"
  Height = 4
  Length = 6
  Placement = pos=(57,-53,14) rot=(0,0,1;0rad)
  Width = 1
FEATURE [Part::Chamfer] Chamfer171
  Base = -> Box798
  Edges = 1 edges r=0.99: [Edge10]
FEATURE [Part::Fillet] Fillet316
  Base = -> Chamfer171
  Edges = 1 edges r=0.99: [Edge8]
FEATURE [Part::Box] Box799  label="Cube980"
  Height = 4
  Length = 4
  Placement = pos=(58,-53.5,14) rot=(0,0,1;0rad)
  Width = 1
FEATURE [Part::Cut] Cut014289
  Base = -> Fillet316
  Placement = pos=(252,45,6) rot=(0,0,1;0rad)
  Tool = -> Box799
FEATURE [Part::Box] Box800  label="Cube981"
  Height = 4
  Length = 6
  Placement = pos=(57,-53,14) rot=(0,0,1;0rad)
  Width = 1
FEATURE [Part::Chamfer] Chamfer172
  Base = -> Box800
  Edges = 1 edges r=0.99: [Edge10]
FEATURE [Part::Fillet] Fillet317
  Base = -> Chamfer172
  Edges = 1 edges r=0.99: [Edge8]
FEATURE [Part::Box] Box801  label="Cube982"
  Height = 4
  Length = 4
  Placement = pos=(58,-53.5,14) rot=(0,0,1;0rad)
  Width = 1
FEATURE [Part::Cut] Cut014290
  Base = -> Fillet317
  Placement = pos=(391,45,6) rot=(0,0,1;0rad)
  Tool = -> Box801
FEATURE [Part::Box] Box802  label="Cube983"
  Height = 4
  Length = 6
  Placement = pos=(57,-53,14) rot=(0,0,1;0rad)
  Width = 1
FEATURE [Part::Chamfer] Chamfer173
  Base = -> Box802
  Edges = 1 edges r=0.99: [Edge10]
FEATURE [Part::Fillet] Fillet318
  Base = -> Chamfer173
  Edges = 1 edges r=0.99: [Edge8]
FEATURE [Part::Box] Box803  label="Cube984"
  Height = 4
  Length = 4
  Placement = pos=(58,-53.5,14) rot=(0,0,1;0rad)
  Width = 1
FEATURE [Part::Cut] Cut014291
  Base = -> Fillet318
  Placement = pos=(459,45,6) rot=(0,0,1;0rad)
  Tool = -> Box803
FEATURE [Part::MultiFuse] Fusion362
  Shapes = -> [Cut014287,Cut014288,Cut014290,Cut014289,Cut014291]
FEATURE [Part::Box] Box804  label="Cube985"
  Height = 5
  Length = 4
  Placement = pos=(531,1,66) rot=(0,0,1;0rad)
  Width = 10
FEATURE [Part::Chamfer] Chamfer174
  Base = -> Box804
  Edges = 1 edges r=4.999: [Edge12]
  Placement = pos=(232.5,528,0) rot=(0,0,-1;1.5708rad)
FEATURE [Part::Box] Box805  label="Cube986"
  Height = 5
  Length = 4
  Placement = pos=(531,159,66) rot=(0,0,1;0rad)
  Width = 10
FEATURE [Part::Chamfer] Chamfer175
  Base = -> Box805
  Edges = 1 edges r=4.999: [Edge10]
  Placement = pos=(357.5,528,0) rot=(0,0,-1;1.5708rad)
FEATURE [Part::Cylinder] Cylinder1171  label="Cylinder1339"
  Angle = 360
  Height = 5
  Placement = pos=(233.5,-5,68.5) rot=(0,1,0;1.5708rad)
  Radius = 0.9
FEATURE [Part::Cylinder] Cylinder1172  label="Cylinder1340"
  Angle = 360
  Height = 5
  Placement = pos=(521.5,-5,68.5) rot=(0,1,0;1.5708rad)
  Radius = 0.9
FEATURE [Part::MultiFuse] Fusion363
  Shapes = -> [Cylinder1171,Cylinder1172]
FEATURE [Part::MultiFuse] Fusion364
  Placement = pos=(482.5,-3,5) rot=(0,0,1;1.5708rad)
  Shapes = -> [Chamfer165,Chamfer167,Chamfer166,Chamfer168]
FEATURE [Part::MultiFuse] Fusion365
  Shapes = -> [Box793,Chamfer175,Chamfer174,Fusion362,Fusion364]
FEATURE [Part::Cut] Cut014292
  Base = -> Fusion365
  Tool = -> Fusion363
FEATURE [Part::Chamfer] Chamfer176
  Base = -> Cut014292
  Edges = 1 edges: [Edge41 r1=1.5 r2=3]
FEATURE [Part::Cylinder] Cylinder1173  label="Cylinder1341"
  Angle = 360
  Height = 2
  Placement = pos=(525,-5,24) rot=(-1,0,0;1.5708rad)
  Radius = 1.6
FEATURE [Part::Cylinder] Cylinder1174  label="Cylinder1342"
  Angle = 360
  Height = 2
  Placement = pos=(235,-5,24) rot=(-1,0,0;1.5708rad)
  Radius = 1.6
FEATURE [Part::MultiFuse] Fusion366
  Shapes = -> [Cylinder1173,Cylinder1174]
FEATURE [Part::Cut] Cut014293
  Base = -> Chamfer176
  Tool = -> Fusion366
FEATURE [Part::Fillet] Fillet319  label="kipper-left-side-wall001"
  Base = -> Cut014293
  Edges = 1 edges r=2: [Edge5]
FEATURE [Part::Mirroring] Part__Mirroring044  label="kipper-right-side-wall"
  Base = (0,0,0)
  Normal = (0,1,0)
  Placement = pos=(0,170,0) rot=(0,0,1;0rad)
  Source = -> Fillet319
FEATURE [Part::Cylinder] Cylinder1175  label="Cylinder1343"
  Angle = 360
  Height = 2
  Placement = pos=(525,-5,24) rot=(-1,0,0;1.5708rad)
  Radius = 1.6
FEATURE [Part::Cylinder] Cylinder1176  label="Cylinder1344"
  Angle = 360
  Height = 2
  Placement = pos=(235,-5,24) rot=(-1,0,0;1.5708rad)
  Radius = 1.6
FEATURE [Part::Cut] Cut014294
  Base = -> Cut014280
  Tool = -> Cylinder1175
FEATURE [Part::Cut] Cut014295  label="kipper-side-wall-rear"
  Base = -> Cut014294
  Tool = -> Fusion359
FEATURE [Part::Cut] Cut014296
  Base = -> Cut014279
  Tool = -> Cylinder1176
FEATURE [Part::Cut] Cut014297  label="kipper-side-wall-front"
  Base = -> Cut014296
  Tool = -> Fusion358
FEATURE [Part::Cylinder] Cylinder1177  label="Cylinder1345"
  Angle = 360
  Height = 2
  Placement = pos=(531,167,24) rot=(0,1,0;1.5708rad)
  Radius = 1.6
FEATURE [Part::MultiFuse] Fusion367
  Shapes = -> [Cylinder1168,Cylinder1177]
FEATURE [Part::Cut] Cut014298
  Base = -> Chamfer125
  Tool = -> Fusion367
FEATURE [Part::Fillet] Fillet320  label="kipper-rear-wall"
  Base = -> Cut014298
  Edges = 1 edges r=2: [Edge5]
FEATURE [Part::Cylinder] Cylinder1178  label="Cylinder1346"
  Angle = 360
  Height = 170
  Placement = pos=(285,170,7) rot=(1,0,0;1.5708rad)
  Radius = 5
FEATURE [Part::MultiFuse] Fusion368
  Shapes = -> [Box603,Box602,Cylinder1019,Cylinder1178]
FEATURE [Part::Fillet] Fillet  label="kipper-frame-ALU_"
  Base = -> Fusion368
  Edges = 2 edges r=5: [Edge59,Edge60]
FEATURE [Part::Box] Box806  label="Cube987"
  Height = 18
  Length = 2
  Placement = pos=(502,0,2) rot=(0,0,1;0rad)
  Width = 10
FEATURE [Part::Box] Box807  label="Cube988"
  Height = 8
  Length = 2
  Placement = pos=(502,10,12) rot=(0,0,1;0rad)
  Width = 15
FEATURE [Part::MultiFuse] Fusion369
  Shapes = -> [Box806,Box807]
FEATURE [Part::Cylinder] Cylinder1179  label="Cylinder1347"
  Angle = 360
  Height = 10
  Placement = pos=(500,5,7) rot=(0,1,0;1.5708rad)
  Radius = 1.75
FEATURE [Part::Cut] Cut014299
  Base = -> Fusion369
  Tool = -> Cylinder1179
FEATURE [Part::Cylinder] Cylinder1180  label="Cylinder1348"
  Angle = 360
  Height = 10
  Placement = pos=(504,4,16) rot=(0,1,0;1.5708rad)
  Radius = 1.6
FEATURE [Part::Cylinder] Cylinder1181  label="Cylinder1349"
  Angle = 360
  Height = 10
  Placement = pos=(504,19,16) rot=(0,1,0;1.5708rad)
  Radius = 1.6
FEATURE [Part::MultiFuse] Fusion370
  Placement = pos=(-4,0,0) rot=(0,0,1;0rad)
  Shapes = -> [Cylinder1181,Cylinder1180]
FEATURE [Part::Cut] Cut014300
  Base = -> Cut014299
  Tool = -> Fusion370
FEATURE [Part::Fillet] Fillet321
  Base = -> Cut014300
  Edges = 2 edges r=4: [Edge1,Edge6]
FEATURE [Part::Fillet] Fillet322  label="kipper-lock-rear-00"
  Base = -> Fillet321
  Edges = 3 edges r=2: [Edge3,Edge17,Edge28]
  Placement = pos=(12,0,0) rot=(0,0,1;0rad)
FEATURE [Part::Box] Box808  label="Cube989"
  Height = 18
  Length = 2
  Placement = pos=(502,0,2) rot=(0,0,1;0rad)
  Width = 10
FEATURE [Part::Box] Box809  label="Cube990"
  Height = 8
  Length = 2
  Placement = pos=(502,10,12) rot=(0,0,1;0rad)
  Width = 15
FEATURE [Part::MultiFuse] Fusion371
  Shapes = -> [Box808,Box809]
FEATURE [Part::Cylinder] Cylinder1182  label="Cylinder1350"
  Angle = 360
  Height = 10
  Placement = pos=(500,5,7) rot=(0,1,0;1.5708rad)
  Radius = 1.75
FEATURE [Part::Cut] Cut014301
  Base = -> Fusion371
  Tool = -> Cylinder1182
FEATURE [Part::Cylinder] Cylinder1183  label="Cylinder1351"
  Angle = 360
  Height = 10
  Placement = pos=(504,4,16) rot=(0,1,0;1.5708rad)
  Radius = 1.6
FEATURE [Part::Cylinder] Cylinder1184  label="Cylinder1352"
  Angle = 360
  Height = 10
  Placement = pos=(504,19,16) rot=(0,1,0;1.5708rad)
  Radius = 1.6
FEATURE [Part::MultiFuse] Fusion372
  Placement = pos=(-4,0,0) rot=(0,0,1;0rad)
  Shapes = -> [Cylinder1184,Cylinder1183]
FEATURE [Part::Cut] Cut014302
  Base = -> Cut014301
  Tool = -> Fusion372
FEATURE [Part::Fillet] Fillet323
  Base = -> Cut014302
  Edges = 2 edges r=4: [Edge1,Edge6]
FEATURE [Part::Fillet] Fillet324  label="kipper-lock-rear"
  Base = -> Fillet323
  Edges = 3 edges r=2: [Edge3,Edge17,Edge28]
FEATURE [Part::MultiFuse] Fusion373
  Shapes = -> [Fillet322,Fillet291]
FEATURE [Part::Box] Box810  label="Cube991"
  Height = 18
  Length = 2
  Placement = pos=(502,0,2) rot=(0,0,1;0rad)
  Width = 10
FEATURE [Part::Box] Box811  label="Cube992"
  Height = 8
  Length = 2
  Placement = pos=(502,10,12) rot=(0,0,1;0rad)
  Width = 15
FEATURE [Part::MultiFuse] Fusion374
  Shapes = -> [Box810,Box811]
FEATURE [Part::Cylinder] Cylinder1185  label="Cylinder1353"
  Angle = 360
  Height = 10
  Placement = pos=(500,5,7) rot=(0,1,0;1.5708rad)
  Radius = 1.75
FEATURE [Part::Cut] Cut014303
  Base = -> Fusion374
  Tool = -> Cylinder1185
FEATURE [Part::Cylinder] Cylinder1186  label="Cylinder1354"
  Angle = 360
  Height = 10
  Placement = pos=(504,4,16) rot=(0,1,0;1.5708rad)
  Radius = 1.6
FEATURE [Part::Cylinder] Cylinder1187  label="Cylinder1355"
  Angle = 360
  Height = 10
  Placement = pos=(504,19,16) rot=(0,1,0;1.5708rad)
  Radius = 1.6
FEATURE [Part::MultiFuse] Fusion375
  Placement = pos=(-4,0,0) rot=(0,0,1;0rad)
  Shapes = -> [Cylinder1187,Cylinder1186]
FEATURE [Part::Cut] Cut014304
  Base = -> Cut014303
  Tool = -> Fusion375
FEATURE [Part::Fillet] Fillet325
  Base = -> Cut014304
  Edges = 2 edges r=4: [Edge1,Edge6]
FEATURE [Part::Fillet] Fillet326  label="kipper-lock-front001"
  Base = -> Fillet325
  Edges = 3 edges r=2: [Edge3,Edge17,Edge28]
  Placement = pos=(-0.5,0,0) rot=(0,0,1;0rad)
FEATURE [Part::Box] Box812  label="Cube993"
  Height = 18
  Length = 2
  Placement = pos=(502,0,2) rot=(0,0,1;0rad)
  Width = 10
FEATURE [Part::Box] Box813  label="Cube994"
  Height = 8
  Length = 2
  Placement = pos=(502,10,12) rot=(0,0,1;0rad)
  Width = 15
FEATURE [Part::MultiFuse] Fusion376
  Shapes = -> [Box812,Box813]
FEATURE [Part::Cylinder] Cylinder1188  label="Cylinder1356"
  Angle = 360
  Height = 10
  Placement = pos=(500,5,7) rot=(0,1,0;1.5708rad)
  Radius = 1.75
FEATURE [Part::Cut] Cut014305
  Base = -> Fusion376
  Tool = -> Cylinder1188
FEATURE [Part::Cylinder] Cylinder1189  label="Cylinder1357"
  Angle = 360
  Height = 10
  Placement = pos=(504,4,16) rot=(0,1,0;1.5708rad)
  Radius = 1.6
FEATURE [Part::Cylinder] Cylinder1190  label="Cylinder1358"
  Angle = 360
  Height = 10
  Placement = pos=(504,19,16) rot=(0,1,0;1.5708rad)
  Radius = 1.6
FEATURE [Part::MultiFuse] Fusion377
  Placement = pos=(-4,0,0) rot=(0,0,1;0rad)
  Shapes = -> [Cylinder1190,Cylinder1189]
FEATURE [Part::Cut] Cut014306
  Base = -> Cut014305
  Tool = -> Fusion377
FEATURE [Part::Fillet] Fillet327
  Base = -> Cut014306
  Edges = 2 edges r=4: [Edge1,Edge6]
FEATURE [Part::Fillet] Fillet328  label="kipper-lock-rear001"
  Base = -> Fillet327
  Edges = 3 edges r=2: [Edge3,Edge17,Edge28]
  Placement = pos=(12.5,0,0) rot=(0,0,1;0rad)
FEATURE [Part::MultiFuse] Fusion378
  Placement = pos=(-224,0,0) rot=(0,0,1;0rad)
  Shapes = -> [Fillet328,Fillet326]
FEATURE [Part::MultiFuse] Fusion379
  Shapes = -> [Fusion378,Fusion373]
FEATURE [Part::Box] Box814  label="Cube995"
  Height = 18
  Length = 2
  Placement = pos=(502,0,2) rot=(0,0,1;0rad)
  Width = 10
FEATURE [Part::Box] Box815  label="Cube996"
  Height = 8
  Length = 2
  Placement = pos=(502,10,12) rot=(0,0,1;0rad)
  Width = 15
FEATURE [Part::MultiFuse] Fusion380
  Shapes = -> [Box814,Box815]
FEATURE [Part::Cylinder] Cylinder1191  label="Cylinder1359"
  Angle = 360
  Height = 10
  Placement = pos=(500,5,7) rot=(0,1,0;1.5708rad)
  Radius = 1.75
FEATURE [Part::Cut] Cut014307
  Base = -> Fusion380
  Tool = -> Cylinder1191
FEATURE [Part::Cylinder] Cylinder1192  label="Cylinder1360"
  Angle = 360
  Height = 10
  Placement = pos=(504,4,16) rot=(0,1,0;1.5708rad)
  Radius = 1.6
FEATURE [Part::Cylinder] Cylinder1193  label="Cylinder1361"
  Angle = 360
  Height = 10
  Placement = pos=(504,19,16) rot=(0,1,0;1.5708rad)
  Radius = 1.6
FEATURE [Part::MultiFuse] Fusion381
  Placement = pos=(-4,0,0) rot=(0,0,1;0rad)
  Shapes = -> [Cylinder1193,Cylinder1192]
FEATURE [Part::Cut] Cut014308
  Base = -> Cut014307
  Tool = -> Fusion381
FEATURE [Part::Fillet] Fillet329
  Base = -> Cut014308
  Edges = 2 edges r=4: [Edge1,Edge6]
FEATURE [Part::Fillet] Fillet330  label="kipper-lock-front002"
  Base = -> Fillet329
  Edges = 3 edges r=2: [Edge3,Edge17,Edge28]
FEATURE [Part::Box] Box816  label="Cube997"
  Height = 18
  Length = 2
  Placement = pos=(502,0,2) rot=(0,0,1;0rad)
  Width = 10
FEATURE [Part::Box] Box817  label="Cube998"
  Height = 8
  Length = 2
  Placement = pos=(502,10,12) rot=(0,0,1;0rad)
  Width = 15
FEATURE [Part::MultiFuse] Fusion382
  Shapes = -> [Box816,Box817]
FEATURE [Part::Cylinder] Cylinder1194  label="Cylinder1362"
  Angle = 360
  Height = 10
  Placement = pos=(500,5,7) rot=(0,1,0;1.5708rad)
  Radius = 1.75
FEATURE [Part::Cut] Cut014309
  Base = -> Fusion382
  Tool = -> Cylinder1194
FEATURE [Part::Cylinder] Cylinder1195  label="Cylinder1363"
  Angle = 360
  Height = 10
  Placement = pos=(504,4,16) rot=(0,1,0;1.5708rad)
  Radius = 1.6
FEATURE [Part::Cylinder] Cylinder1196  label="Cylinder1364"
  Angle = 360
  Height = 10
  Placement = pos=(504,19,16) rot=(0,1,0;1.5708rad)
  Radius = 1.6
FEATURE [Part::MultiFuse] Fusion383
  Placement = pos=(-4,0,0) rot=(0,0,1;0rad)
  Shapes = -> [Cylinder1196,Cylinder1195]
FEATURE [Part::Cut] Cut014310
  Base = -> Cut014309
  Tool = -> Fusion383
FEATURE [Part::Fillet] Fillet331
  Base = -> Cut014310
  Edges = 2 edges r=4: [Edge1,Edge6]
FEATURE [Part::Fillet] Fillet332  label="kipper-lock-rear002"
  Base = -> Fillet331
  Edges = 3 edges r=2: [Edge3,Edge17,Edge28]
  Placement = pos=(12,0,0) rot=(0,0,1;0rad)
FEATURE [Part::MultiFuse] Fusion384
  Shapes = -> [Fillet332,Fillet330]
FEATURE [Part::Box] Box818  label="Cube999"
  Height = 18
  Length = 2
  Placement = pos=(502,0,2) rot=(0,0,1;0rad)
  Width = 10
FEATURE [Part::Box] Box819  label="Cube1000"
  Height = 8
  Length = 2
  Placement = pos=(502,10,12) rot=(0,0,1;0rad)
  Width = 15
FEATURE [Part::MultiFuse] Fusion385
  Shapes = -> [Box818,Box819]
FEATURE [Part::Cylinder] Cylinder1197  label="Cylinder1365"
  Angle = 360
  Height = 10
  Placement = pos=(500,5,7) rot=(0,1,0;1.5708rad)
  Radius = 1.75
FEATURE [Part::Cut] Cut014311
  Base = -> Fusion385
  Tool = -> Cylinder1197
FEATURE [Part::Cylinder] Cylinder1198  label="Cylinder1366"
  Angle = 360
  Height = 10
  Placement = pos=(504,4,16) rot=(0,1,0;1.5708rad)
  Radius = 1.6
FEATURE [Part::Cylinder] Cylinder1199  label="Cylinder1367"
  Angle = 360
  Height = 10
  Placement = pos=(504,19,16) rot=(0,1,0;1.5708rad)
  Radius = 1.6
FEATURE [Part::MultiFuse] Fusion386
  Placement = pos=(-4,0,0) rot=(0,0,1;0rad)
  Shapes = -> [Cylinder1199,Cylinder1198]
FEATURE [Part::Cut] Cut014312
  Base = -> Cut014311
  Tool = -> Fusion386
FEATURE [Part::Fillet] Fillet333
  Base = -> Cut014312
  Edges = 2 edges r=4: [Edge1,Edge6]
FEATURE [Part::Fillet] Fillet334  label="kipper-lock-front003"
  Base = -> Fillet333
  Edges = 3 edges r=2: [Edge3,Edge17,Edge28]
  Placement = pos=(-0.5,0,0) rot=(0,0,1;0rad)
FEATURE [Part::Box] Box820  label="Cube1001"
  Height = 18
  Length = 2
  Placement = pos=(502,0,2) rot=(0,0,1;0rad)
  Width = 10
FEATURE [Part::Box] Box821  label="Cube1002"
  Height = 8
  Length = 2
  Placement = pos=(502,10,12) rot=(0,0,1;0rad)
  Width = 15
FEATURE [Part::MultiFuse] Fusion387
  Shapes = -> [Box820,Box821]
FEATURE [Part::Cylinder] Cylinder1200  label="Cylinder1368"
  Angle = 360
  Height = 10
  Placement = pos=(500,5,7) rot=(0,1,0;1.5708rad)
  Radius = 1.75
FEATURE [Part::Cut] Cut014313
  Base = -> Fusion387
  Tool = -> Cylinder1200
FEATURE [Part::Cylinder] Cylinder1201  label="Cylinder1369"
  Angle = 360
  Height = 10
  Placement = pos=(504,4,16) rot=(0,1,0;1.5708rad)
  Radius = 1.6
FEATURE [Part::Cylinder] Cylinder1202  label="Cylinder1370"
  Angle = 360
  Height = 10
  Placement = pos=(504,19,16) rot=(0,1,0;1.5708rad)
  Radius = 1.6
FEATURE [Part::MultiFuse] Fusion388
  Placement = pos=(-4,0,0) rot=(0,0,1;0rad)
  Shapes = -> [Cylinder1202,Cylinder1201]
FEATURE [Part::Cut] Cut014314
  Base = -> Cut014313
  Tool = -> Fusion388
FEATURE [Part::Fillet] Fillet335
  Base = -> Cut014314
  Edges = 2 edges r=4: [Edge1,Edge6]
FEATURE [Part::Fillet] Fillet336  label="kipper-lock-rear003"
  Base = -> Fillet335
  Edges = 3 edges r=2: [Edge3,Edge17,Edge28]
  Placement = pos=(12.5,0,0) rot=(0,0,1;0rad)
FEATURE [Part::MultiFuse] Fusion389
  Placement = pos=(-224,0,0) rot=(0,0,1;0rad)
  Shapes = -> [Fillet336,Fillet334]
FEATURE [Part::MultiFuse] Fusion390
  Shapes = -> [Fusion389,Fusion384]
FEATURE [Part::Mirroring] Part__Mirroring045  label="Fusion390 (Mirror #10)"
  Base = (0,0,0)
  Normal = (0,1,0)
  Placement = pos=(0,170,0) rot=(0,0,1;0rad)
  Source = -> Fusion390
FEATURE [Part::MultiFuse] Fusion391  label="kipper-locks"
  Shapes = -> [Part__Mirroring045,Fusion379]
FEATURE [Part::Cylinder] Cylinder1203  label="Cylinder1371"
  Angle = 360
  Height = 10
  Placement = pos=(509,0,8) rot=(-1,0,0;1.5708rad)
  Radius = 6.5
FEATURE [Part::Fillet] Fillet337
  Base = -> Cylinder1203
  Edges = 2 edges r=2: [Edge1,Edge3]
FEATURE [Part::Cylinder] Cylinder1204  label="Cylinder1372"
  Angle = 360
  Height = 10
  Placement = pos=(509,0,8) rot=(-1,0,0;1.5708rad)
  Radius = 6.5
FEATURE [Part::Fillet] Fillet338
  Base = -> Cylinder1204
  Edges = 2 edges r=2: [Edge1,Edge3]
  Placement = pos=(0,160,0) rot=(0,0,1;0rad)
FEATURE [Part::MultiFuse] Fusion392
  Placement = pos=(-224,0,0) rot=(0,0,1;0rad)
  Shapes = -> [Fillet338,Fillet337]
FEATURE [Part::Cylinder] Cylinder1205  label="Cylinder1373"
  Angle = 360
  Height = 10
  Placement = pos=(509,0,8) rot=(-1,0,0;1.5708rad)
  Radius = 6.5
FEATURE [Part::Fillet] Fillet339
  Base = -> Cylinder1205
  Edges = 2 edges r=2: [Edge1,Edge3]
FEATURE [Part::Cylinder] Cylinder1206  label="Cylinder1374"
  Angle = 360
  Height = 10
  Placement = pos=(509,0,8) rot=(-1,0,0;1.5708rad)
  Radius = 6.5
FEATURE [Part::Fillet] Fillet340
  Base = -> Cylinder1206
  Edges = 2 edges r=2: [Edge1,Edge3]
  Placement = pos=(0,160,0) rot=(0,0,1;0rad)
FEATURE [Part::MultiFuse] Fusion393
  Shapes = -> [Fillet340,Fillet339]
FEATURE [Part::Cylinder] Cylinder050
  Angle = 360
  Height = 20
  Placement = pos=(390,85,4.5) rot=(0,1,0;1.5708rad)
  Radius = 20.5
FEATURE [Part::Cylinder] Cylinder051
  Angle = 360
  Height = 10
  Placement = pos=(400,85,12) rot=(0,1,0;1.5708rad)
  Radius = 7
FEATURE [Part::Cylinder] Cylinder052
  Angle = 360
  Height = 75
  Placement = pos=(331,85,5) rot=(0,1,0;1.5708rad)
  Radius = 18.7
FEATURE [Part::Cylinder] Cylinder053
  Angle = 360
  Height = 10
  Placement = pos=(15.5,0,0) rot=(0,0,1;0rad)
  Radius = 1.6
FEATURE [Part::Cylinder] Cylinder054
  Angle = 360
  Height = 10
  Placement = pos=(-15.5,0,0) rot=(0,0,1;0rad)
  Radius = 1.6
FEATURE [Part::MultiFuse] Fusion041
  Placement = pos=(0,0,0) rot=(0,0,1;1.0472rad)
  Shapes = -> [Cylinder054,Cylinder053]
FEATURE [Part::Cylinder] Cylinder055
  Angle = 360
  Height = 10
  Placement = pos=(15.5,0,0) rot=(0,0,1;0rad)
  Radius = 1.6
FEATURE [Part::Cylinder] Cylinder056
  Angle = 360
  Height = 10
  Placement = pos=(-15.5,0,0) rot=(0,0,1;0rad)
  Radius = 1.6
FEATURE [Part::MultiFuse] Fusion042
  Placement = pos=(0,0,0) rot=(0,0,1;2.0944rad)
  Shapes = -> [Cylinder056,Cylinder055]
FEATURE [Part::Cylinder] Cylinder057
  Angle = 360
  Height = 10
  Placement = pos=(-15.5,0,0) rot=(0,0,1;0rad)
  Radius = 1.6
FEATURE [Part::Cylinder] Cylinder058
  Angle = 360
  Height = 10
  Placement = pos=(15.5,0,0) rot=(0,0,1;0rad)
  Radius = 1.6
FEATURE [Part::MultiFuse] Fusion043
  Shapes = -> [Cylinder057,Cylinder058]
FEATURE [Part::MultiFuse] Fusion044
  Placement = pos=(0,0,0) rot=(0,0,1;0.523599rad)
  Shapes = -> [Fusion041,Fusion042,Fusion043]
FEATURE [Part::Box] Box023  label="Cube002"
  Height = 10
  Length = 10
  Width = 10
FEATURE [Part::Cut] Cut026  label="holes"
  Base = -> Fusion044
  Placement = pos=(408,85,2) rot=(0,1,0;1.5708rad)
  Tool = -> Box023
FEATURE [Part::Cylinder] Cylinder059
  Angle = 360
  Height = 22
  Placement = pos=(417,85,5) rot=(0,1,0;1.5708rad)
  Radius = 18.7
FEATURE [Part::Cylinder] Cylinder060
  Angle = 360
  Height = 31
  Placement = pos=(439,85,5) rot=(0,1,0;1.5708rad)
  Radius = 17.5
FEATURE [Part::Cut] Cut014319
  Base = -> Cylinder050
  Tool = -> Cylinder052
FEATURE [Part::Cut] Cut014320
  Base = -> Cut014319
  Placement = pos=(823,170,-3) rot=(0,0,1;3.14159rad)
  Tool = -> Cylinder051
FEATURE [Part::Cylinder] Cylinder1207  label="Cylinder1375"
  Angle = 360
  Height = 6
  Placement = pos=(411,85,12) rot=(0,1,0;1.5708rad)
  Radius = 7
FEATURE [Part::Cylinder] Cylinder1208  label="Cylinder1376"
  Angle = 360
  Height = 150
  Placement = pos=(290,85,12) rot=(0,1,0;1.5708rad)
  Radius = 4
FEATURE [Part::Cylinder] Cylinder1209  label="Cylinder1377"
  Angle = 360
  Height = 170
  Placement = pos=(469,170,19.5) rot=(1,0,0;1.5708rad)
  Radius = 1
FEATURE [Part::Box] Box822  label="Cube1003"
  Height = 18
  Length = 2.5
  Placement = pos=(502,0,2) rot=(0,0,1;0rad)
  Width = 10
FEATURE [Part::Box] Box823  label="Cube1004"
  Height = 8
  Length = 2.5
  Placement = pos=(502,10,12) rot=(0,0,1;0rad)
  Width = 15
FEATURE [Part::MultiFuse] Fusion395
  Shapes = -> [Box822,Box823]
FEATURE [Part::Cylinder] Cylinder1210  label="Cylinder1378"
  Angle = 360
  Height = 10
  Placement = pos=(500,5,7) rot=(0,1,0;1.5708rad)
  Radius = 1.75
FEATURE [Part::Cut] Cut014322
  Base = -> Fusion395
  Tool = -> Cylinder1210
FEATURE [Part::Cylinder] Cylinder1211  label="Cylinder1379"
  Angle = 360
  Height = 10
  Placement = pos=(504,4,16) rot=(0,1,0;1.5708rad)
  Radius = 1.6
FEATURE [Part::Cylinder] Cylinder1212  label="Cylinder1380"
  Angle = 360
  Height = 10
  Placement = pos=(504,19,16) rot=(0,1,0;1.5708rad)
  Radius = 1.6
FEATURE [Part::MultiFuse] Fusion396
  Placement = pos=(-4,0,0) rot=(0,0,1;0rad)
  Shapes = -> [Cylinder1212,Cylinder1211]
FEATURE [Part::Cut] Cut014323
  Base = -> Cut014322
  Tool = -> Fusion396
FEATURE [Part::Fillet] Fillet341
  Base = -> Cut014323
  Edges = 2 edges r=4: [Edge1,Edge6]
FEATURE [Part::Fillet] Fillet342  label="kipper-lock-front-left_"
  Base = -> Fillet341
  Edges = 3 edges r=2: [Edge3,Edge17,Edge28]
  Placement = pos=(-211.5,0,0) rot=(0,0,1;0rad)
FEATURE [Part::Cylinder] Cylinder1213  label="Cylinder1381"
  Angle = 360
  Height = 10
  Placement = pos=(285,0,6) rot=(-1,0,0;1.5708rad)
  Radius = 6
FEATURE [Part::Box] Box824  label="Cube1005"
  Height = 10
  Length = 12
  Placement = pos=(279,0,-4) rot=(0,0,1;0rad)
  Width = 10
FEATURE [Part::MultiFuse] Fusion397
  Shapes = -> [Cylinder1213,Box824]
FEATURE [Part::Cut] Cut014324
  Base = -> Fillet342
  Tool = -> Fusion397
FEATURE [Part::Chamfer] Chamfer178
  Base = -> Cut014324
  Edges = 1 edges r=0.5: [Edge15]
FEATURE [Part::Box] Box825  label="Cube1006"
  Height = 10
  Length = 13
  Placement = pos=(280,0,-5) rot=(0,-1,0;0.261799rad)
  Width = 10
FEATURE [Part::Cut] Cut014325  label="kipper-lock-front-left"
  Base = -> Chamfer178
  Tool = -> Box825
FEATURE [Part::Box] Box826  label="Cube1007"
  Height = 18
  Length = 2.5
  Placement = pos=(502,0,2) rot=(0,0,1;0rad)
  Width = 10
FEATURE [Part::Box] Box827  label="Cube1008"
  Height = 8
  Length = 2.5
  Placement = pos=(502,10,12) rot=(0,0,1;0rad)
  Width = 15
FEATURE [Part::MultiFuse] Fusion398
  Shapes = -> [Box826,Box827]
FEATURE [Part::Cylinder] Cylinder1214  label="Cylinder1382"
  Angle = 360
  Height = 10
  Placement = pos=(500,5,7) rot=(0,1,0;1.5708rad)
  Radius = 1.75
FEATURE [Part::Cut] Cut014326
  Base = -> Fusion398
  Tool = -> Cylinder1214
FEATURE [Part::Cylinder] Cylinder1215  label="Cylinder1383"
  Angle = 360
  Height = 10
  Placement = pos=(504,4,16) rot=(0,1,0;1.5708rad)
  Radius = 1.6
FEATURE [Part::Cylinder] Cylinder1216  label="Cylinder1384"
  Angle = 360
  Height = 10
  Placement = pos=(504,19,16) rot=(0,1,0;1.5708rad)
  Radius = 1.6
FEATURE [Part::MultiFuse] Fusion399
  Placement = pos=(-4,0,0) rot=(0,0,1;0rad)
  Shapes = -> [Cylinder1216,Cylinder1215]
FEATURE [Part::Cut] Cut014327
  Base = -> Cut014326
  Tool = -> Fusion399
FEATURE [Part::Fillet] Fillet343
  Base = -> Cut014327
  Edges = 2 edges r=4: [Edge1,Edge6]
FEATURE [Part::Fillet] Fillet344  label="kipper-lock-front-left_001"
  Base = -> Fillet343
  Edges = 3 edges r=2: [Edge3,Edge17,Edge28]
  Placement = pos=(-211.5,0,0) rot=(0,0,1;0rad)
FEATURE [Part::Cylinder] Cylinder1217  label="Cylinder1385"
  Angle = 360
  Height = 10
  Placement = pos=(285,0,6) rot=(-1,0,0;1.5708rad)
  Radius = 6
FEATURE [Part::Box] Box828  label="Cube1009"
  Height = 10
  Length = 12
  Placement = pos=(279,0,-4) rot=(0,0,1;0rad)
  Width = 10
FEATURE [Part::MultiFuse] Fusion400
  Shapes = -> [Cylinder1217,Box828]
FEATURE [Part::Cut] Cut014328
  Base = -> Fillet344
  Tool = -> Fusion400
FEATURE [Part::Chamfer] Chamfer179
  Base = -> Cut014328
  Edges = 1 edges r=0.5: [Edge15]
FEATURE [Part::Box] Box829  label="Cube1010"
  Height = 10
  Length = 13
  Placement = pos=(280,0,-5) rot=(0,-1,0;0.261799rad)
  Width = 10
FEATURE [Part::Cut] Cut014329  label="kipper-lock-front-left001"
  Base = -> Chamfer179
  Tool = -> Box829
FEATURE [Part::Mirroring] Part__Mirroring046  label="kipper-lock-front-right"
  Base = (0,0,0)
  Normal = (1,0,0)
  Placement = pos=(570,0,0) rot=(0,0,1;0rad)
  Source = -> Cut014329
FEATURE [Part::Box] Box830  label="Cube1011"
  Height = 14
  Length = 14
  Placement = pos=(278,55,0) rot=(0,0,1;0rad)
  Width = 60
FEATURE [Part::Cylinder] Cylinder1218  label="Cylinder1386"
  Angle = 360
  Height = 14
  Placement = pos=(0,60,7) rot=(0,1,0;1.5708rad)
  Radius = 2.5
FEATURE [Part::Cylinder] Cylinder1219  label="Cylinder1387"
  Angle = 360
  Height = 14
  Placement = pos=(0,110,7) rot=(0,1,0;1.5708rad)
  Radius = 2.5
FEATURE [Part::MultiFuse] Fusion401
  Placement = pos=(275,0,0) rot=(0,0,1;0rad)
  Shapes = -> [Cylinder1219,Cylinder1218]
FEATURE [Part::Cylinder] Cylinder1220  label="Cylinder1388"
  Angle = 360
  Height = 170
  Placement = pos=(285,170,7) rot=(1,0,0;1.5708rad)
  Radius = 5.1
FEATURE [Part::MultiFuse] Fusion402
  Shapes = -> [Fusion401,Cylinder1220]
FEATURE [Part::Cut] Cut014330  label="kipper-frame-ALU-HOLES-00"
  Base = -> Box830
  Tool = -> Fusion402
FEATURE [Part::Box] Box831  label="Cube928"
  Height = 17
  Length = 10
  Placement = pos=(-2,0,1.5) rot=(0,0,1;0rad)
  Width = 60
FEATURE [Part::Fillet] Fillet007070
  Base = -> Box831
  Edges = 4 edges r=3: [Edge9,Edge10,Edge11,Edge12]
  Placement = pos=(485.5,55,-23) rot=(0,0,1;0rad)
FEATURE [Part::Box] Box832  label="Cube929"
  Height = 10
  Length = 10
  Placement = pos=(483.5,63,-7.5) rot=(0,0,1;0rad)
  Width = 44
FEATURE [Part::Cut] Cut014331  label="Cut014449"
  Base = -> Fillet007070
  Tool = -> Box832
FEATURE [Part::Cylinder] Cylinder1236  label="Cylinder1591"
  Angle = 360
  Height = 10
  Placement = pos=(3,60,10) rot=(1,0,0;1.5708rad)
  Radius = 1.2
FEATURE [Part::Cylinder] Cylinder1237  label="Cylinder1592"
  Angle = 360
  Height = 10
  Placement = pos=(3,10,10) rot=(1,0,0;1.5708rad)
  Radius = 1.2
FEATURE [Part::MultiFuse] Fusion248002159  label="Fusion248002266"
  Placement = pos=(485.5,55,-23) rot=(0,0,1;0rad)
  Shapes = -> [Cylinder1236,Cylinder1237]
FEATURE [Part::Chamfer] Chamfer180
  Base = -> Cut014331
  Edges = 2 edges r=2.99: [Edge18,Edge25]
FEATURE [Part::Cut] Cut014332  label="Cut014450"
  Base = -> Chamfer180
  Placement = pos=(18,0,5) rot=(0,0,1;0rad)
  Tool = -> Fusion248002159
FEATURE [Part::Cylinder] Cylinder1238  label="Cylinder1593"
  Angle = 360
  Height = 10
  Placement = pos=(483.5,85,-14.5) rot=(0,1,0;1.5708rad)
  Radius = 2.6
FEATURE [Part::Cylinder] Cylinder1239  label="Cylinder1594"
  Angle = 360
  Height = 10
  Placement = pos=(483.5,79,-10.5) rot=(0,1,0;1.5708rad)
  Radius = 1.2
FEATURE [Part::Cylinder] Cylinder1240  label="Cylinder1595"
  Angle = 360
  Height = 10
  Placement = pos=(483.5,91,-10.5) rot=(0,1,0;1.5708rad)
  Radius = 1.2
FEATURE [Part::Cylinder] Cylinder1241  label="Cylinder1596"
  Angle = 360
  Height = 10
  Placement = pos=(483.5,79,-18.5) rot=(0,1,0;1.5708rad)
  Radius = 1.2
FEATURE [Part::Cylinder] Cylinder1242  label="Cylinder1597"
  Angle = 360
  Height = 10
  Placement = pos=(483.5,91,-18.5) rot=(0,1,0;1.5708rad)
  Radius = 1.2
FEATURE [Part::MultiFuse] Fusion248002160  label="Fusion248002267"
  Placement = pos=(18,0,5) rot=(0,0,1;0rad)
  Shapes = -> [Cylinder1238,Cylinder1242,Cylinder1239,Cylinder1240,Cylinder1241]
FEATURE [Part::Cut] Cut014333  label="Cut014451"
  Base = -> Cut014332
  Placement = pos=(0.5,0,0) rot=(0,0,1;0rad)
  Tool = -> Fusion248002160
FEATURE [Part::Cylinder] Cylinder1262  label="Cylinder1616"
  Angle = 360
  Height = 10
  Placement = pos=(509,61,-10.5) rot=(0,1,0;1.5708rad)
  Radius = 1.1
FEATURE [Part::Cylinder] Cylinder1263  label="Cylinder1617"
  Angle = 360
  Height = 10
  Placement = pos=(509,58,-14.5) rot=(0,1,0;1.5708rad)
  Radius = 1.1
FEATURE [Part::MultiFuse] Fusion248002174  label="Fusion248002280"
  Placement = pos=(-7,0,0) rot=(0,0,1;0rad)
  Shapes = -> [Cylinder1263,Cylinder1262]
FEATURE [Part::Cylinder] Cylinder1264  label="Cylinder1618"
  Angle = 360
  Height = 10
  Placement = pos=(509,64,-14.5) rot=(0,1,0;1.5708rad)
  Radius = 1.1
FEATURE [Part::Cylinder] Cylinder1265  label="Cylinder1619"
  Angle = 360
  Height = 10
  Placement = pos=(509,61,-10.5) rot=(0,1,0;1.5708rad)
  Radius = 1.1
FEATURE [Part::MultiFuse] Fusion248002175  label="Fusion248002281"
  Placement = pos=(-7,48,0) rot=(0,0,1;0rad)
  Shapes = -> [Cylinder1264,Cylinder1265]
FEATURE [Part::MultiFuse] Fusion248002176  label="Fusion248002282"
  Shapes = -> [Fusion248002175,Fusion248002174]
FEATURE [Part::Cut] Cut014334  label="Cut014459"
  Base = -> Cut014333
  Tool = -> Fusion248002176
FEATURE [Part::Box] Box833  label="Cube1012"
  Height = 3
  Length = 10
  Placement = pos=(502,55,-11.5) rot=(0,0,1;0rad)
  Width = 4
FEATURE [Part::Box] Box834  label="Cube1013"
  Height = 3
  Length = 10
  Placement = pos=(502,111,-11.5) rot=(0,0,1;0rad)
  Width = 4
FEATURE [Part::MultiFuse] Fusion248002177  label="Fusion248002283"
  Placement = pos=(0,0,-1) rot=(0,0,1;0rad)
  Shapes = -> [Box833,Box834]
FEATURE [Part::Fillet] Fillet007073
  Base = -> Fusion248002177
  Edges = 4 edges r=1: [Edge9,Edge10,Edge23,Edge24]
FEATURE [Part::Cut] Cut014335  label="cross-member-rear"
  Base = -> Cut014334
  Tool = -> Fillet007073
FEATURE [Part::MultiFuse] Fusion248002200  label="kipper-spindle-motor"
  Placement = pos=(0.821678,0,-27.5671) rot=(0,-1,0;0.05236rad)
  Shapes = -> [Cylinder1207,Cylinder059,Cylinder060,Cylinder1208]
FEATURE [Part::Box] Box835  label="Cube1014"
  Height = 1
  Length = 10
  Placement = pos=(423,65,21) rot=(0,0,1;0rad)
  Width = 40
FEATURE [Part::Box] Box836  label="Cube1015"
  Height = 1.5
  Length = 10
  Placement = pos=(423,65,-19) rot=(0,0,1;0rad)
  Width = 40
FEATURE [Part::Box] Box837  label="Cube1016"
  Height = 41
  Length = 20
  Placement = pos=(413,64,-19) rot=(0,0,1;0rad)
  Width = 1
FEATURE [Part::Box] Box838  label="Cube1017"
  Height = 41
  Length = 20
  Placement = pos=(413,105,-19) rot=(0,0,1;0rad)
  Width = 1
FEATURE [Part::MultiFuse] Fusion248002201
  Shapes = -> [Box838,Box836,Box837,Box835]
FEATURE [Part::Cut] Cut014336
  Base = -> Cut014320
  Tool = -> Cut026
FEATURE [Part::Cut] Cut014337
  Base = -> Cut014336
  Placement = pos=(0.66467,0,-24.5712) rot=(0,-1,0;0.05236rad)
  Tool = -> Fusion248002201
FEATURE [Part::Cylinder] Cylinder1267  label="Cylinder1647"
  Angle = 360
  Height = 108
  Placement = pos=(300,85,0) rot=(0,1,0;1.43117rad)
  Radius = 2.5
FEATURE [Part::MultiFuse] Fusion248002202
  Shapes = -> [Cylinder1088,Cylinder1089]
FEATURE [Part::MultiFuse] Fusion248002203
  Shapes = -> [Fusion248002202,Fusion285,Fusion282,Fusion283]
FEATURE [Part::Cut] Cut014338
  Base = -> Fusion279
  Tool = -> Fusion248002203
FEATURE [Part::Cut] Cut014339
  Base = -> Cut014338
  Tool = -> Box
FEATURE [Part::Cut] Cut014340
  Base = -> Cut014339
  Tool = -> Fusion393
FEATURE [Part::MultiFuse] Fusion248002204
  Shapes = -> [Cylinder1112,Cylinder1111]
FEATURE [Part::MultiFuse] Fusion248002205
  Shapes = -> [Fusion248002204,Fusion291,Fusion294,Fusion292]
FEATURE [Part::Cut] Cut014342
  Base = -> Fusion290
  Tool = -> Fusion248002205
FEATURE [Part::Cut] Cut014343
  Base = -> Cut014342
  Tool = -> Box660
FEATURE [Part::Cut] Cut014344
  Base = -> Cut014343
  Tool = -> Fusion392
FEATURE [Part::Cut] Cut014345
  Base = -> Cut014344
  Tool = -> Fusion297
FEATURE [Part::Box] Box840  label="Cube1019"
  Height = 4
  Length = 10
  Placement = pos=(375,70,12) rot=(0,0,1;0rad)
  Width = 30
FEATURE [Part::Cut] Cut014346
  Base = -> Cut014345
  Tool = -> Box840
FEATURE [Part::Chamfer] Chamfer181  label="kipper-frame-front"
  Base = -> Cut014346
  Edges = 2 edges r=3.99: [Edge3,Edge114]
FEATURE [Part::Cylinder] Cylinder1268  label="Cylinder1648"
  Angle = 360
  Height = 60
  Placement = pos=(405,115,15) rot=(1,0,0;1.5708rad)
  Radius = 3
FEATURE [Part::Box] Box841  label="Cube1020"
  Height = 5
  Length = 6
  Placement = pos=(402,55,15) rot=(0,0,1;0rad)
  Width = 60
FEATURE [Part::MultiFuse] Fusion248002206
  Shapes = -> [Box841,Cylinder1268]
FEATURE [Part::Cylinder] Cylinder1269  label="Cylinder1649"
  Angle = 360
  Height = 60
  Placement = pos=(405,115,15) rot=(1,0,0;1.5708rad)
  Radius = 1.6
FEATURE [Part::Cut] Cut014347
  Base = -> Cut014340
  Tool = -> Fusion296
FEATURE [Part::MultiFuse] Fusion248002207
  Shapes = -> [Cut014347,Fusion248002206]
FEATURE [Part::Cut] Cut014348
  Base = -> Fusion248002207
  Tool = -> Cylinder1269
FEATURE [Part::Box] Box842  label="Cube1021"
  Height = 7.6
  Length = 6
  Placement = pos=(402,81.5,12) rot=(0,0,1;0rad)
  Width = 7
FEATURE [Part::Cut] Cut014349  label="kipper-frame-rear"
  Base = -> Cut014348
  Tool = -> Box842
FEATURE [Part::Cylinder] Cylinder1270  label="Cylinder1650"
  Angle = 360
  Height = 4
  Placement = pos=(297,85,9) rot=(0,1,0;1.5708rad)
  Radius = 5.6
FEATURE [Part::Box] Box843  label="Cube1022"
  Height = 8
  Length = 10
  Placement = pos=(290,65,9) rot=(0,0,1;0rad)
  Width = 40
FEATURE [Part::Cylinder] Cylinder1271  label="Cylinder1651"
  Angle = 360
  Height = 10
  Placement = pos=(290,85,9) rot=(0,1,0;1.5708rad)
  Radius = 8
FEATURE [Part::MultiFuse] Fusion248002208
  Shapes = -> [Cylinder1271,Box843]
FEATURE [Part::Cut] Cut014350
  Base = -> Fusion248002208
  Placement = pos=(-0.33396,0,-24.6235) rot=(0,-1,0;0.05236rad)
  Tool = -> Cylinder1270
FEATURE [Part::Box] Box845  label="Cube1024"
  Height = 25
  Length = 4
  Placement = pos=(286,65,-8.5) rot=(0,0,1;0rad)
  Width = 40
FEATURE [Part::Cut] Cut014351
  Base = -> Cut014350
  Tool = -> Box845
FEATURE [Part::Chamfer] Chamfer182
  Base = -> Cut014351
  Edges = 2 edges r=5: [Edge6,Edge19]
FEATURE [Part::Box] Box846  label="Cube1025"
  Height = 12.5
  Length = 15
  Placement = pos=(290,65,-0.5) rot=(0,0,1;0rad)
  Width = 8
FEATURE [Part::Box] Box847  label="Cube1026"
  Height = 12.5
  Length = 15
  Placement = pos=(290,97,-0.5) rot=(0,0,1;0rad)
  Width = 8
FEATURE [Part::MultiFuse] Fusion248002209
  Shapes = -> [Chamfer182,Box846,Box847]
FEATURE [Part::Chamfer] Chamfer183
  Base = -> Fusion248002209
  Edges = 2 edges r=3: [Edge13,Edge38]
FEATURE [Part::Cylinder] Cylinder1272  label="Cylinder1652"
  Angle = 360
  Height = 10
  Placement = pos=(293,72,7.5) rot=(1,0,0;1.5708rad)
  Radius = 1.5
FEATURE [Part::Cylinder] Cylinder1273  label="Cylinder1653"
  Angle = 360
  Height = 10
  Placement = pos=(302,72,7.5) rot=(1,0,0;1.5708rad)
  Radius = 1.5
FEATURE [Part::MultiFuse] Fusion248002210
  Placement = pos=(0,36,0) rot=(0,0,1;0rad)
  Shapes = -> [Cylinder1272,Cylinder1273]
FEATURE [Part::Cylinder] Cylinder1274  label="Cylinder1656"
  Angle = 360
  Height = 10
  Placement = pos=(293,72,7.5) rot=(1,0,0;1.5708rad)
  Radius = 1.5
FEATURE [Part::Cylinder] Cylinder1275  label="Cylinder1657"
  Angle = 360
  Height = 10
  Placement = pos=(302,72,7.5) rot=(1,0,0;1.5708rad)
  Radius = 1.5
FEATURE [Part::MultiFuse] Fusion248002211
  Shapes = -> [Cylinder1274,Cylinder1275]
FEATURE [Part::MultiFuse] Fusion248002212
  Shapes = -> [Fusion248002210,Fusion248002211]
FEATURE [Part::Cut] Cut014352  label="kipper-motor-rod-holder_"
  Base = -> Chamfer183
  Tool = -> Fusion248002212
FEATURE [Part::Box] Box848  label="Cube1027"
  Height = 10
  Length = 30
  Placement = pos=(401,65,2) rot=(0,0,1;0rad)
  Width = 8
FEATURE [Part::Cylinder] Cylinder1276  label="Cylinder1658"
  Angle = 360
  Height = 20
  Placement = pos=(413.02,85,-1.45848) rot=(0,1,0;1.51844rad)
  Radius = 20.5
FEATURE [Part::Box] Box849  label="Cube1028"
  Height = 10
  Length = 30
  Placement = pos=(401,97,2) rot=(0,0,1;0rad)
  Width = 8
FEATURE [Part::MultiFuse] Fusion248002213
  Shapes = -> [Box848,Box849]
FEATURE [Part::Cut] Cut014353
  Base = -> Fusion248002213
  Tool = -> Cylinder1276
FEATURE [Part::MultiFuse] Fusion248002214
  Shapes = -> [Cut014353,Cut014337]
FEATURE [Part::Cylinder] Cylinder1278  label="Cylinder1664"
  Angle = 360
  Height = 10
  Placement = pos=(317,72,7.5) rot=(1,0,0;1.5708rad)
  Radius = 1.25
FEATURE [Part::Cylinder] Cylinder1279  label="Cylinder1665"
  Angle = 360
  Height = 10
  Placement = pos=(293,72,7.5) rot=(1,0,0;1.5708rad)
  Radius = 1.25
FEATURE [Part::Cylinder] Cylinder1280  label="Cylinder1666"
  Angle = 360
  Height = 10
  Placement = pos=(303,72,7.5) rot=(1,0,0;1.5708rad)
  Radius = 1.25
FEATURE [Part::MultiFuse] Fusion248002215
  Placement = pos=(111,1,0) rot=(0,0,1;0rad)
  Shapes = -> [Cylinder1278,Cylinder1280,Cylinder1279]
FEATURE [Part::Cylinder] Cylinder1281  label="Cylinder1670"
  Angle = 360
  Height = 10
  Placement = pos=(317,72,7.5) rot=(1,0,0;1.5708rad)
  Radius = 1.25
FEATURE [Part::Cylinder] Cylinder1282  label="Cylinder1671"
  Angle = 360
  Height = 10
  Placement = pos=(293,72,7.5) rot=(1,0,0;1.5708rad)
  Radius = 1.25
FEATURE [Part::Cylinder] Cylinder1283  label="Cylinder1672"
  Angle = 360
  Height = 10
  Placement = pos=(303,72,7.5) rot=(1,0,0;1.5708rad)
  Radius = 1.25
FEATURE [Part::MultiFuse] Fusion248002216
  Placement = pos=(111,35,0) rot=(0,0,1;0rad)
  Shapes = -> [Cylinder1281,Cylinder1283,Cylinder1282]
FEATURE [Part::MultiFuse] Fusion248002217
  Shapes = -> [Fusion248002216,Fusion248002215]
FEATURE [Part::Cut] Cut014354  label="kipper-motor-holder"
  Base = -> Fusion248002214
  Tool = -> Fusion248002217
FEATURE [Part::Cylinder] Cylinder1284  label="Cylinder1675"
  Angle = 360
  Height = 10
  Placement = pos=(293,72,7.5) rot=(1,0,0;1.5708rad)
  Radius = 1.5
FEATURE [Part::Cylinder] Cylinder1285  label="Cylinder1676"
  Angle = 360
  Height = 10
  Placement = pos=(302,72,7.5) rot=(1,0,0;1.5708rad)
  Radius = 1.5
FEATURE [Part::MultiFuse] Fusion248002218
  Shapes = -> [Cylinder1284,Cylinder1285]
FEATURE [Part::Cylinder] Cylinder1286  label="Cylinder1680"
  Angle = 360
  Height = 10
  Placement = pos=(317,72,7.5) rot=(1,0,0;1.5708rad)
  Radius = 1.25
FEATURE [Part::Cylinder] Cylinder1287  label="Cylinder1681"
  Angle = 360
  Height = 10
  Placement = pos=(293,72,7.5) rot=(1,0,0;1.5708rad)
  Radius = 1.25
FEATURE [Part::Cylinder] Cylinder1288  label="Cylinder1682"
  Angle = 360
  Height = 10
  Placement = pos=(303,72,7.5) rot=(1,0,0;1.5708rad)
  Radius = 1.25
FEATURE [Part::Box] Box850  label="Cube1029"
  Height = 16
  Length = 15
  Placement = pos=(290,58,-1) rot=(0,0,1;0rad)
  Width = 10
FEATURE [Part::Box] Box851  label="Cube1030"
  Height = 10.4
  Length = 15
  Placement = pos=(290,55,1.8) rot=(0,0,1;0rad)
  Width = 10
FEATURE [Part::Cut] Cut014355
  Base = -> Box850
  Tool = -> Box851
FEATURE [Part::Box] Box852  label="Cube1031"
  Height = 16
  Length = 30
  Placement = pos=(290,58,-1) rot=(0,0,1;0rad)
  Width = 10
FEATURE [Part::Box] Box853  label="Cube1032"
  Height = 10.4
  Length = 30
  Placement = pos=(290,55,1.8) rot=(0,0,1;0rad)
  Width = 10
FEATURE [Part::Cut] Cut014356
  Base = -> Box852
  Placement = pos=(111,0,0) rot=(0,0,1;0rad)
  Tool = -> Box853
FEATURE [Part::Cut] Cut014357  label="kipper-motor-rod-holder-HOLES"
  Base = -> Cut014355
  Tool = -> Fusion248002218
FEATURE [Part::Cylinder] Cylinder1289  label="Cylinder1683"
  Angle = 360
  Height = 10
  Placement = pos=(307,72,7.5) rot=(1,0,0;1.5708rad)
  Radius = 1.25
FEATURE [Part::MultiFuse] Fusion248002219
  Placement = pos=(111,0,0) rot=(0,0,1;0rad)
  Shapes = -> [Cylinder1286,Cylinder1288,Cylinder1287,Cylinder1289]
FEATURE [Part::Cut] Cut014358  label="kipper-motor-holder-HOLES"
  Base = -> Cut014356
  Tool = -> Fusion248002219
FEATURE [Part::Box] Box854  label="Cube1033"
  Height = 10
  Length = 69
  Placement = pos=(211,105,2) rot=(0,0,1;0rad)
  Width = 10
FEATURE [Part::Box] Box855  label="Cube1034"
  Height = 10
  Length = 69
  Placement = pos=(211,55,2) rot=(0,0,1;0rad)
  Width = 10
FEATURE [Part::MultiFuse] Fusion248002220  label="kipper-frame-ALU"
  Shapes = -> [Fillet,Box854,Box855]
FEATURE [Part::Box] Box856  label="Cube1035"
  Height = 14
  Length = 10
  Placement = pos=(211,65,-1) rot=(0,0,1;0rad)
  Width = 40
FEATURE [Part::Box] Box857  label="Cube1036"
  Height = 2
  Length = 10
  Placement = pos=(211,63,12) rot=(0,0,1;0rad)
  Width = 44
FEATURE [Part::MultiFuse] Fusion248002221  label="kipper-frame-ALU-HOLES-01"
  Shapes = -> [Box857,Box856]
FEATURE [Part::RegularPolygon] RegularPolygon  label="Regular polygon"
  Circumradius = 7.5
  Polygon = 6
FEATURE [Part::Feature] Face
  shape: bbox 22.54 x 22.54 x 2e-07 mm, 1 faces, 0 solids (baked)
FEATURE [Part::Extrusion] Extrude  label="kipper-lifter-hex-screw-STEEL"
  Base = -> Face
  Dir = (0,0,8)
  Placement = pos=(300.627,85,0.06083) rot=(0,1,0;1.51844rad)
  Solid = false
FEATURE [Part::Cylinder] Cylinder1290  label="Cylinder1684"
  Angle = 360
  Height = 170
  Placement = pos=(304,170,13) rot=(1,0,0;1.5708rad)
  Radius = 3.05
FEATURE [Part::Cylinder] Cylinder1291  label="Cylinder1685"
  Angle = 360
  Height = 170
  Placement = pos=(405,170,15) rot=(1,0,0;1.5708rad)
  Radius = 1.5
FEATURE [Part::Box] Box858  label="Cube1037"
  Height = 10
  Length = 74
  Placement = pos=(299,73.5,8) rot=(0,0,1;0rad)
  Width = 5
FEATURE [Part::Box] Box859  label="Cube1038"
  Height = 10
  Length = 74
  Placement = pos=(299,91.5,8) rot=(0,0,1;0rad)
  Width = 5
FEATURE [Part::Cylinder] Cylinder1292  label="Cylinder1686"
  Angle = 360
  Height = 7
  Placement = pos=(405,88.5,15) rot=(1,0,0;1.5708rad)
  Radius = 4.5
FEATURE [Part::Cylinder] Cylinder1293  label="Cylinder1687"
  Angle = 360
  Height = 13
  Placement = pos=(389.5,85,15) rot=(0,1,0;1.5708rad)
  Radius = 3
FEATURE [Part::MultiFuse] Fusion248002222
  Shapes = -> [Cylinder1293,Cylinder1292]
FEATURE [Part::Cylinder] Cylinder1294  label="Cylinder1688"
  Angle = 360
  Height = 170
  Placement = pos=(405,170,15) rot=(1,0,0;1.5708rad)
  Radius = 1.5
FEATURE [Part::Cut] Cut014359  label="kipper-lifter-arm-head-ALU"
  Base = -> Fusion248002222
  Placement = pos=(4.84685,0,-49.2453) rot=(0,-1,0;0.122173rad)
  Tool = -> Cylinder1294
FEATURE [Part::Box] Box860  label="Cube1039"
  Height = 6
  Length = 41
  Placement = pos=(348.5,78.5,12) rot=(0,0,1;0rad)
  Width = 13
FEATURE [Part::Cylinder] Cylinder1295  label="Cylinder1689"
  Angle = 360
  Height = 13
  Placement = pos=(379.5,85,15) rot=(0,1,0;1.5708rad)
  Radius = 1.6
FEATURE [Part::Chamfer] Chamfer184
  Base = -> Box859
  Edges = 1 edges: [Edge8 r1=4 r2=30]
FEATURE [Part::Chamfer] Chamfer185
  Base = -> Box858
  Edges = 1 edges: [Edge8 r1=4 r2=30]
FEATURE [Part::MultiFuse] Fusion248002223
  Shapes = -> [Chamfer184,Chamfer185,Box860]
FEATURE [Part::Chamfer] Chamfer187
  Base = -> Fusion248002223
  Edges = 2 edges: [Edge14 r1=4.99 r2=30,Edge22 r1=4.99 r2=30]
FEATURE [Part::Chamfer] Chamfer188
  Base = -> Chamfer187
  Edges = 2 edges r=3: [Edge11,Edge35]
FEATURE [Part::Fillet] Fillet007074
  Base = -> Chamfer188
  Edges = 4 edges r=3: [Edge22,Edge29,Edge46,Edge53]
FEATURE [Part::Cut] Cut014360
  Base = -> Fillet007074
  Tool = -> Cylinder1290
FEATURE [Part::Box] Box861  label="Cube1040"
  Height = 6
  Length = 31
  Placement = pos=(348.5,81.9,12) rot=(0,0,1;0rad)
  Width = 6.2
FEATURE [Part::Cut] Cut014361
  Base = -> Cut014360
  Tool = -> Box861
FEATURE [Part::Cut] Cut014362
  Base = -> Cut014361
  Tool = -> Cylinder1295
FEATURE [Part::Chamfer] Chamfer189
  Base = -> Cut014362
  Edges = 2 edges r=3.39: [Edge53,Edge70]
  Placement = pos=(4.84685,0,-49.2453) rot=(0,-1,0;0.122173rad)
FEATURE [Part::Cylinder] Cylinder1296  label="Cylinder1690"
  Angle = 360
  Height = 150
  Placement = pos=(290.638,85,-0.357858) rot=(0,1,0;1.51844rad)
  Radius = 4.5
FEATURE [Part::Cut] Cut014363  label="kipper-lifter-arm_00"
  Base = -> Chamfer189
  Tool = -> Cylinder1296
FEATURE [Part::Cylinder] Cylinder1297  label="Cylinder1694"
  Angle = 360
  Height = 170
  Placement = pos=(304,170,13) rot=(1,0,0;1.5708rad)
  Radius = 3.05
FEATURE [Part::Box] Box862  label="Cube1041"
  Height = 10
  Length = 74
  Placement = pos=(299,73.5,8) rot=(0,0,1;0rad)
  Width = 5
FEATURE [Part::Box] Box863  label="Cube1042"
  Height = 10
  Length = 74
  Placement = pos=(299,91.5,8) rot=(0,0,1;0rad)
  Width = 5
FEATURE [Part::Box] Box864  label="Cube1043"
  Height = 6
  Length = 41
  Placement = pos=(348.5,78.5,12) rot=(0,0,1;0rad)
  Width = 13
FEATURE [Part::Cylinder] Cylinder1298  label="Cylinder1695"
  Angle = 360
  Height = 13
  Placement = pos=(379.5,85,15) rot=(0,1,0;1.5708rad)
  Radius = 1.6
FEATURE [Part::Chamfer] Chamfer190
  Base = -> Box863
  Edges = 1 edges: [Edge8 r1=4 r2=30]
FEATURE [Part::Chamfer] Chamfer191
  Base = -> Box862
  Edges = 1 edges: [Edge8 r1=4 r2=30]
FEATURE [Part::MultiFuse] Fusion248002224
  Shapes = -> [Chamfer190,Chamfer191,Box864]
FEATURE [Part::Chamfer] Chamfer192
  Base = -> Fusion248002224
  Edges = 2 edges: [Edge14 r1=4.99 r2=30,Edge22 r1=4.99 r2=30]
FEATURE [Part::Chamfer] Chamfer193
  Base = -> Chamfer192
  Edges = 2 edges r=3: [Edge11,Edge35]
FEATURE [Part::Fillet] Fillet007075
  Base = -> Chamfer193
  Edges = 4 edges r=3: [Edge22,Edge29,Edge46,Edge53]
FEATURE [Part::Cut] Cut014364
  Base = -> Fillet007075
  Tool = -> Cylinder1297
FEATURE [Part::Box] Box865  label="Cube1044"
  Height = 6
  Length = 31
  Placement = pos=(348.5,81.9,12) rot=(0,0,1;0rad)
  Width = 6.2
FEATURE [Part::Cut] Cut014365
  Base = -> Cut014364
  Tool = -> Box865
FEATURE [Part::Cut] Cut014366
  Base = -> Cut014365
  Tool = -> Cylinder1298
FEATURE [Part::Cylinder] Cylinder1299  label="Cylinder1696"
  Angle = 360
  Height = 150
  Placement = pos=(290.638,85,-0.357858) rot=(0,1,0;1.51844rad)
  Radius = 4.5
FEATURE [Part::Fillet] Fillet007076  label="kipper-motor-rod-holder"
  Base = -> Cut014352
  Edges = 2 edges r=4: [Edge5,Edge47]
FEATURE [Part::Box] Box866  label="Cube1045"
  Height = 1
  Length = 33
  Placement = pos=(316,78.5,17) rot=(0,0,1;0rad)
  Width = 13
FEATURE [Part::Box] Box867  label="Cube1046"
  Height = 10
  Length = 10
  Placement = pos=(297,63,8) rot=(0,0,1;0.785398rad)
  Width = 10
FEATURE [Part::Box] Box868  label="Cube1047"
  Height = 10
  Length = 10
  Placement = pos=(297,93,8) rot=(0,0,1;0.785398rad)
  Width = 10
FEATURE [Part::MultiFuse] Fusion248002225
  Shapes = -> [Box868,Box867]
FEATURE [Part::Cut] Cut014367
  Base = -> Cut014366
  Tool = -> Fusion248002225
FEATURE [Part::MultiFuse] Fusion248002226
  Placement = pos=(4.84685,0,-49.2453) rot=(0,-1,0;0.122173rad)
  Shapes = -> [Box866,Cut014367]
FEATURE [Part::Cut] Cut014368  label="kipper-lifter-arm"
  Base = -> Fusion248002226
  Tool = -> Cylinder1299
